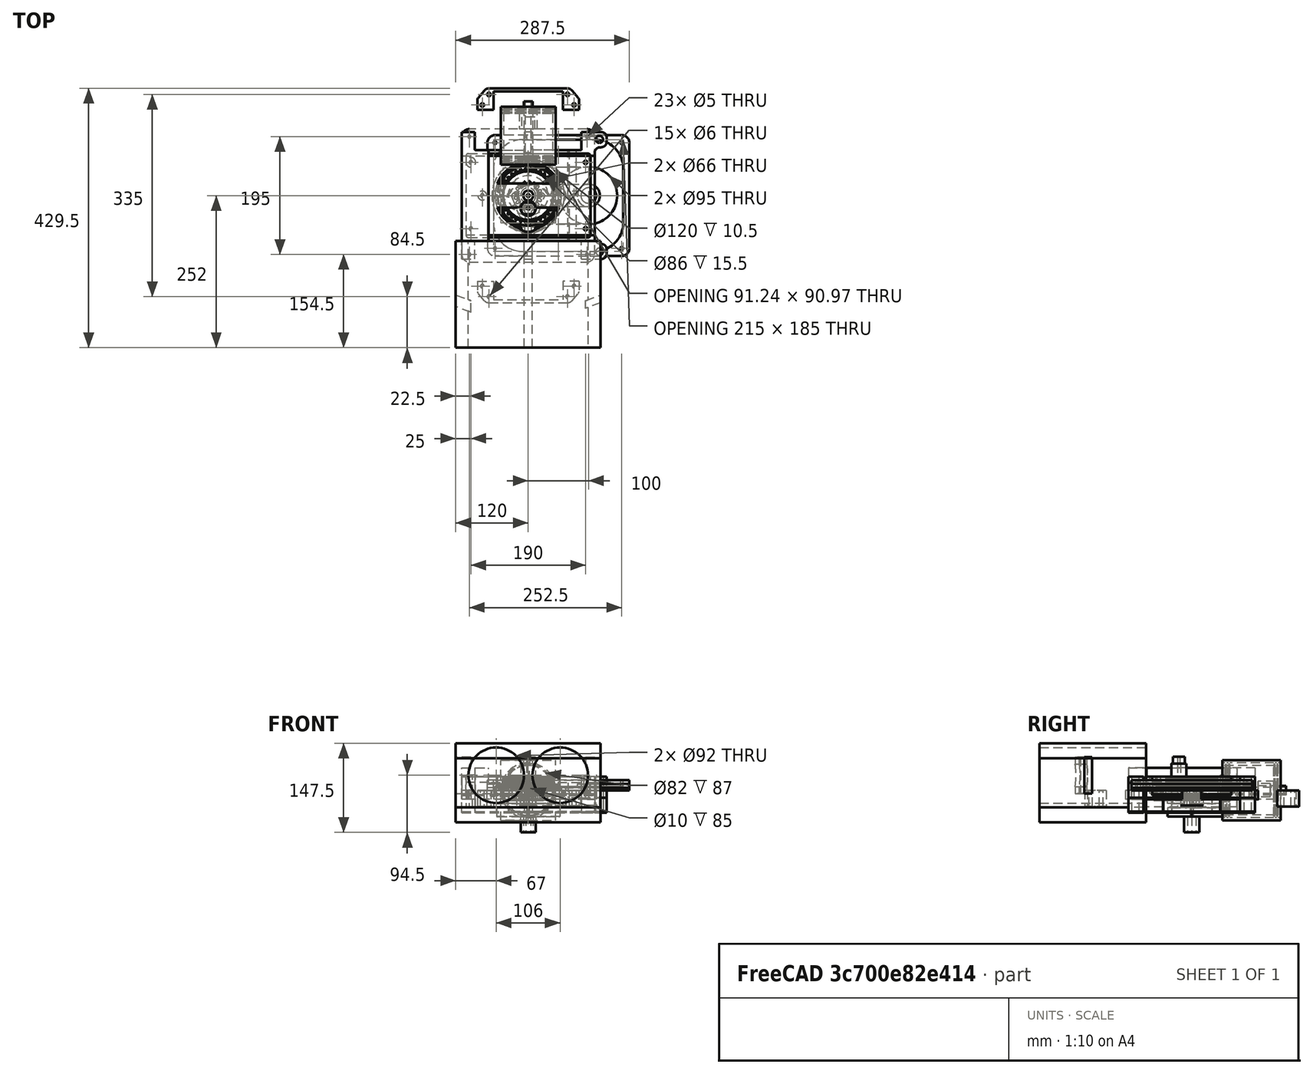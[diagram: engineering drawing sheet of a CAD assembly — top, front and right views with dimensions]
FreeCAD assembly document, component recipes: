
FREECAD ASSEMBLY — COMPONENT RECIPES ("assm4_XX_at_Tusi_rider")

This assembly document has 31 components, labeled P0..P30 below (a component is one placed body or linked part). 30 of them carry a construction recipe — the FreeCAD feature program that regenerates the part from scratch, quoted from this document or its linked companion documents; the rest are supplied as boundary geometry only. No exploded tour is included for this assembly.
COMPONENT P0 — geometry summary ("Assembly_total"; no construction recipe available for this part):
  bounding box: 314.5 x 312.0 x 154.5 mm
  tessellated surface: 128,050 triangles
  volume: 581524 mm^3 (4% of its bounding box)
COMPONENT P1 — recipe-attached ("Шток_поршня", modeled in this document).
Construction recipe (the document's own serialized feature program — sketch geometry with constraints, then the solid features built on it; lengths are millimeters unless a unit is written):

FEATURE [PartDesign::CoordinateSystem] Pin
  AttacherType = Attacher::AttachEngine3D
  AttachmentSupport = -> [XY_Plane001]
  MapMode = 5
FEATURE [Sketcher::SketchObject] Sketch053
  ArcFitTolerance = 0
  AttachmentOffset = pos=(0,0,-66) rot=(0,0,1;0rad)
  AttachmentSupport = -> [XZ_Plane001]
  FullyConstrained = true
  MakeInternals = false
  MapMode = 5
  Placement = pos=(0,66,-1.47e-14) rot=(1,0,0;1.5708rad)
  sketch-geometry (2):
    g0: Circle CenterX=0 CenterY=0 CenterZ=0 NormalX=0 NormalY=0 NormalZ=1 AngleXU=0 Radius=7.5
    g1: Circle CenterX=0 CenterY=0 CenterZ=0 NormalX=0 NormalY=0 NormalZ=1 AngleXU=0 Radius=5
  constraints (4):
    c: Coincident(g0,g-1)
    c: Coincident(g1,g0)
    c: Diameter(g0) = 15
    c: Diameter(g1) = 10
FEATURE [PartDesign::Pad] Pad
  Direction = (0,-1,2e-16)
  Length = 90
  Length2 = 1
  Placement = pos=(0,0,0) rot=(1,0,0;1.5708rad)
  Profile = -> Sketch053
  ReferenceAxis = -> Sketch053 [N_Axis]
  Reversed = true
  Suppressed = false
  Type = 0
FEATURE [Sketcher::SketchObject] Sketch055
  ArcFitTolerance = 0
  AttachmentOffset = pos=(0,0,-66) rot=(0,0,1;0rad)
  AttachmentSupport = -> [XZ_Plane001]
  FullyConstrained = true
  MakeInternals = false
  MapMode = 5
  Placement = pos=(0,66,-1.47e-14) rot=(1,0,0;1.5708rad)
  sketch-geometry (2):
    g0: Circle CenterX=0 CenterY=0 CenterZ=0 NormalX=0 NormalY=0 NormalZ=1 AngleXU=0 Radius=5
    g1: Circle CenterX=0 CenterY=0 CenterZ=0 NormalX=0 NormalY=0 NormalZ=1 AngleXU=0 Radius=2
  constraints (4):
    c: Diameter(g0) = 10
    c: Coincident(g1,g0)
    c: Coincident(g0,g-1)
    c: Diameter(g1) = 4
FEATURE [PartDesign::Pad] Pad026
  BaseFeature = -> Pad
  Direction = (0,-1,2e-16)
  Length = 5
  Length2 = 17
  Placement = pos=(0,0,0) rot=(1,0,0;1.5708rad)
  Profile = -> Sketch055
  ReferenceAxis = -> Sketch055 [N_Axis]
  Reversed = true
  Suppressed = false
  Type = 4
FEATURE [Sketcher::SketchObject] Sketch085
  ArcFitTolerance = 1e-06
  AttachmentOffset = pos=(0,0,-66) rot=(0,0,1;0rad)
  AttachmentSupport = -> [XZ_Plane001]
  ExternalGeometry = -> [Pad026]
  FullyConstrained = true
  MakeInternals = false
  MapMode = 5
  Placement = pos=(0,66,-1.47e-14) rot=(1,0,0;1.5708rad)
  sketch-geometry (7):
    g0: ArcOfCircle CenterX=0 CenterY=0 CenterZ=0 NormalX=0 NormalY=0 NormalZ=1 AngleXU=0 Radius=7.5 StartAngle=2.41186 EndAngle=3.87132
    g1: LineSegment StartX=-5.59017 StartY=5 StartZ=0 EndX=5.59017 EndY=5 EndZ=0
    g2: LineSegment StartX=-5.59017 StartY=-5 StartZ=0 EndX=5.59017 EndY=-5 EndZ=0
    g3: ArcOfCircle CenterX=0 CenterY=0 CenterZ=0 NormalX=0 NormalY=0 NormalZ=1 AngleXU=0 Radius=7.5 StartAngle=5.55346 EndAngle=7.01291
    g4: LineSegment [constr] StartX=0 StartY=5 StartZ=0 EndX=0 EndY=-5 EndZ=0
    g5: LineSegment [constr] StartX=5.59017 StartY=5 StartZ=0 EndX=5.59017 EndY=-5 EndZ=0
    g6: Circle CenterX=0 CenterY=0 CenterZ=0 NormalX=0 NormalY=0 NormalZ=1 AngleXU=0 Radius=2
  constraints (20):
    c: Coincident(g0,g-1)
    c: Horizontal(g1)
    c: Horizontal(g2)
    c: Coincident(g0,g1)
    c: Coincident(g1,g3)
    c: Equal(g0,g3)
    c: Coincident(g0,g2)
    c: Coincident(g0,g3)
    c: Equal(g3,g-3)
    c: PointOnObject(g4,g-5)
    c: PointOnObject(g4,g-5)
    c: Coincident(g5,g1)
    c: Coincident(g5,g2)
    c: Vertical(g5)
    c: Equal(g4,g5)
    c: PointOnObject(g4,g-2)
    c: Coincident(g6,g0)
    c: Equal(g6,g-4)
    c: Coincident(g2,g3)
    c: Vertical(g4)
FEATURE [PartDesign::Pad] Pad046
  BaseFeature = -> Pad026
  Direction = (0,-1,2e-16)
  Length = 2
  Length2 = 10
  Placement = pos=(0,0,0) rot=(1,0,0;1.5708rad)
  Profile = -> Sketch085
  ReferenceAxis = -> Sketch085 [N_Axis]
  Refine = true
  Suppressed = false
  Type = 0
FEATURE [PartDesign::Body] Body  label="Шток_поршня"
  AllowCompound = false
  Group = -> [Pin,Sketch053,Pad,Sketch055,Pad026,Sketch085,Pad046]
  Origin = -> Origin001
  Tip = -> Pad046
COMPONENT P2 — recipe-attached ("Эксцентрик", modeled in this document).
Construction recipe (the document's own serialized feature program — sketch geometry with constraints, then the solid features built on it; lengths are millimeters unless a unit is written):

FEATURE [Sketcher::SketchObject] Sketch005
  ArcFitTolerance = 0
  AttachmentSupport = -> [XY_Plane002]
  FullyConstrained = true
  MakeInternals = false
  MapMode = 5
  expr: Constraints[1] = <<Dim_table>>.crank_dia2 + <<Dim_table>>.zazor
  expr: Constraints[26] = 10
  expr: Constraints[27] = <<Dim_table>>.ecc_dia * 0.8
  expr: Constraints[28] = <<Dim_table>>.crank_dia2 * 2
  expr: Constraints[2] = <<Dim_table>>.ecc_dia + <<Dim_table>>.roller_dia
  expr: Constraints[3] = <<Dim_table>>.crank_len
  sketch-geometry (14):
    g0: Circle CenterX=0 CenterY=-21.25 CenterZ=0 NormalX=0 NormalY=0 NormalZ=1 AngleXU=0 Radius=41.5
    g1: Circle CenterX=0 CenterY=0 CenterZ=0 NormalX=0 NormalY=0 NormalZ=1 AngleXU=0 Radius=12.75
    g2: ArcOfCircle CenterX=0 CenterY=-21.25 CenterZ=0 NormalX=0 NormalY=0 NormalZ=1 AngleXU=0 Radius=32 StartAngle=3.32205 EndAngle=4.38515
    g3: ArcOfCircle CenterX=0 CenterY=-21.25 CenterZ=0 NormalX=0 NormalY=0 NormalZ=1 AngleXU=0 Radius=32 StartAngle=5.03963 EndAngle=6.10273
    g4: LineSegment StartX=-5 StartY=-27.5681 StartZ=0 EndX=-5 EndY=-47.7641 EndZ=0
    g5: LineSegment StartX=5 StartY=-27.5681 StartZ=0 EndX=5 EndY=-47.7641 EndZ=0
    g6: ArcOfCircle CenterX=0 CenterY=0 CenterZ=0 NormalX=0 NormalY=0 NormalZ=1 AngleXU=0 Radius=25 StartAngle=3.98424 EndAngle=4.39683
    g7: ArcOfCircle CenterX=0 CenterY=0 CenterZ=0 NormalX=0 NormalY=0 NormalZ=1 AngleXU=0 Radius=25 StartAngle=5.02794 EndAngle=5.44053
    g8: ArcOfCircle CenterX=-22.6265 CenterY=-25.3779 CenterZ=0 NormalX=0 NormalY=0 NormalZ=1 AngleXU=0 Radius=9 StartAngle=0.842651 EndAngle=3.32205
    g9: ArcOfCircle CenterX=22.6265 CenterY=-25.3779 CenterZ=0 NormalX=0 NormalY=0 NormalZ=1 AngleXU=0 Radius=9 StartAngle=6.10273 EndAngle=8.58213
    g10: ArcOfCircle CenterX=-9 CenterY=-47.7641 CenterZ=0 NormalX=0 NormalY=0 NormalZ=1 AngleXU=0 Radius=4 StartAngle=4.38515 EndAngle=6.28319
    g11: ArcOfCircle CenterX=9 CenterY=-47.7641 CenterZ=0 NormalX=0 NormalY=0 NormalZ=1 AngleXU=0 Radius=4 StartAngle=3.14159 EndAngle=5.03963
    g12: ArcOfCircle CenterX=-9 CenterY=-27.5681 CenterZ=0 NormalX=0 NormalY=0 NormalZ=1 AngleXU=0 Radius=4 StartAngle=0 EndAngle=1.25524
    g13: ArcOfCircle CenterX=9 CenterY=-27.5681 CenterZ=0 NormalX=0 NormalY=0 NormalZ=1 AngleXU=0 Radius=4 StartAngle=1.88635 EndAngle=3.14159
  constraints (32):
    c: PointOnObject(g0,g-2)
    c: Diameter(g1) = 25.5
    c: Diameter(g0) = 83
    c: Distance(g1,g0) = 21.25
    c: Coincident(g1,g-1)
    c: Coincident(g2,g0)
    c: Coincident(g3,g0)
    c: Equal(g2,g3)
    c: Vertical(g4)
    c: Coincident(g6,g1)
    c: Coincident(g7,g1)
    c: Tangent(g2,g8) = -1.5708
    c: Tangent(g6,g8) = 1.5708
    c: Tangent(g7,g9) = 1.5708
    c: Tangent(g3,g9) = -1.5708
    c: Tangent(g2,g10) = -1.5708
    c: Tangent(g4,g10) = 1.5708
    c: Tangent(g5,g11) = -1.5708
    c: Tangent(g3,g11) = -1.5708
    c: Tangent(g6,g12) = 1.5708
    c: Tangent(g4,g12) = 1.5708
    c: Tangent(g5,g13) = -1.5708
    c: Tangent(g7,g13) = 1.5708
    c: Symmetric(g12,g13,g-2)
    c: Symmetric(g10,g11,g-2)
    c: Symmetric(g8,g9,g-2)
    c: DistanceX(g4,g5) = 10
    c: Diameter(g2) = 64
    c: Diameter(g6) = 50
    c: Radius(g10) = 4
    c: Equal(g10,g12)
    c: Radius(g8) = 9
FEATURE [PartDesign::CoordinateSystem] Eccentr
  AttacherType = Attacher::AttachEngine3D
  AttachmentOffset = pos=(0,0,0) rot=(0,0,1;1.5708rad)
  AttachmentSupport = -> [Sketch005]
  MapMode = 11
  Placement = pos=(0,0,0) rot=(0,0,1;3.14159rad)
FEATURE [PartDesign::Pad] Pad001
  Direction = (0,0,1)
  Length = 16.5
  Length2 = 0
  Profile = -> Sketch005
  ReferenceAxis = -> Sketch005 [N_Axis]
  Reversed = true
  Suppressed = false
  Type = 0
  expr: Length = <<Dim_table>>.ecc_hei
FEATURE [PartDesign::SubtractiveCylinder] Cylinder003
  Angle = 360
  AttacherType = Attacher::AttachEngine3D
  AttachmentOffset = pos=(0,0,-14) rot=(0,0,1;0rad)
  AttachmentSupport = -> [Pad001]
  BaseFeature = -> Pad001
  FirstAngle = 0
  Height = 25.2
  MapMode = 2
  Placement = pos=(0,0,-14) rot=(0,0,1;0rad)
  Radius = 16
  Refine = true
  SecondAngle = 0
  Suppressed = false
FEATURE [PartDesign::SubtractiveCylinder] Cylinder008
  Angle = 360
  AttacherType = Attacher::AttachEngine3D
  AttachmentOffset = pos=(23,0,-13) rot=(0,0,1;0rad)
  AttachmentSupport = -> [XY_Plane002]
  BaseFeature = -> Cylinder003
  FirstAngle = 0
  Height = 25
  MapMode = 5
  Placement = pos=(23,0,-13) rot=(0,0,1;0rad)
  Radius = 4
  Refine = true
  SecondAngle = 0
  Suppressed = false
FEATURE [PartDesign::SubtractiveCylinder] Cylinder009
  Angle = 360
  AttacherType = Attacher::AttachEngine3D
  AttachmentOffset = pos=(-23,0,-13) rot=(0,0,1;0rad)
  AttachmentSupport = -> [XY_Plane002]
  BaseFeature = -> Cylinder008
  FirstAngle = 0
  Height = 25
  MapMode = 5
  Placement = pos=(-23,0,-13) rot=(0,0,1;0rad)
  Radius = 4
  Refine = true
  SecondAngle = 0
  Suppressed = false
FEATURE [Sketcher::SketchObject] Sketch084
  ArcFitTolerance = 1e-06
  AttachmentSupport = -> [XY_Plane002]
  FullyConstrained = true
  MakeInternals = false
  MapMode = 5
  expr: Constraints[2] = <<Dim_table>>.crank_len
  expr: Constraints[3] = <<Dim_table>>.ecc_dia
  expr: Constraints[4] = <<Dim_table>>.ecc_dia * 1.2
  sketch-geometry (2):
    g0: Circle CenterX=0 CenterY=-21.25 CenterZ=0 NormalX=0 NormalY=0 NormalZ=1 AngleXU=0 Radius=40
    g1: Circle CenterX=0 CenterY=-21.25 CenterZ=0 NormalX=0 NormalY=0 NormalZ=1 AngleXU=0 Radius=48
  constraints (5):
    c: PointOnObject(g0,g-2)
    c: Coincident(g1,g0)
    c: Distance(g0,g-1) = 21.25
    c: Diameter(g0) = 80
    c: Diameter(g1) = 96
FEATURE [PartDesign::Pocket] Pocket
  BaseFeature = -> Cylinder009
  Direction = (0,0,-1)
  Length = 15.25
  Length2 = -1.25
  Placement = pos=(-23,0,-13) rot=(0,0,1;0rad)
  Profile = -> Sketch084
  ReferenceAxis = -> Sketch084 [N_Axis]
  Refine = true
  Suppressed = false
  Type = 4
FEATURE [PartDesign::Body] Body001  label="Эксцентрик"
  AllowCompound = false
  Group = -> [Sketch005,Pad001,Eccentr,Cylinder003,Cylinder008,Cylinder009,Sketch084,Pocket]
  Origin = -> Origin002
  Tip = -> Pocket
COMPONENT P3 — recipe-attached ("Ползун_рабочий", modeled in this document).
Construction recipe (the document's own serialized feature program — sketch geometry with constraints, then the solid features built on it; lengths are millimeters unless a unit is written):

FEATURE [Sketcher::SketchObject] Sketch007
  ArcFitTolerance = 0
  AttachmentSupport = -> [XY_Plane003]
  FullyConstrained = true
  MakeInternals = false
  MapMode = 5
  expr: Constraints[15] = <<Dim_table>>.ecc_dia * 1.3
  expr: Constraints[17] = <<Dim_table>>.ecc_dia * 0.8
  expr: Constraints[1] = <<Dim_table>>.ecc_dia + 2 * <<Dim_table>>.roller_dia
  sketch-geometry (15):
    g0: Circle CenterX=0 CenterY=0 CenterZ=0 NormalX=0 NormalY=0 NormalZ=1 AngleXU=0 Radius=43
    g1: ArcOfCircle CenterX=0 CenterY=0 CenterZ=0 NormalX=0 NormalY=0 NormalZ=1 AngleXU=0 Radius=52 StartAngle=1.86916 EndAngle=3.14159
    g2: ArcOfCircle CenterX=0 CenterY=0 CenterZ=0 NormalX=0 NormalY=0 NormalZ=1 AngleXU=0 Radius=52 StartAngle=0 EndAngle=1.27243
    g3: LineSegment StartX=-11.8314 StartY=53.6134 StartZ=0 EndX=-10 EndY=64 EndZ=0
    g4: LineSegment StartX=-10 StartY=64 StartZ=0 EndX=10 EndY=64 EndZ=0
    g5: LineSegment StartX=10 StartY=64 StartZ=0 EndX=11.8314 EndY=53.6134 EndZ=0
    g6: ArcOfCircle CenterX=-16.7555 CenterY=54.4817 CenterZ=0 NormalX=0 NormalY=0 NormalZ=1 AngleXU=0 Radius=5 StartAngle=5.01075 EndAngle=6.10865
    g7: ArcOfCircle CenterX=16.7555 CenterY=54.4817 CenterZ=0 NormalX=0 NormalY=0 NormalZ=1 AngleXU=0 Radius=5 StartAngle=3.31613 EndAngle=4.41403
    g8: ArcOfCircle CenterX=-2.7e-15 CenterY=2.94305e-05 CenterZ=0 NormalX=0 NormalY=0 NormalZ=1 AngleXU=0 Radius=52 StartAngle=3.14159 EndAngle=4.41403
    g9: ArcOfCircle CenterX=-16.7555 CenterY=-54.4817 CenterZ=0 NormalX=0 NormalY=0 NormalZ=1 AngleXU=0 Radius=5 StartAngle=0.174533 EndAngle=1.27243
    g10: LineSegment StartX=-11.8314 StartY=-53.6134 StartZ=0 EndX=-10 EndY=-64 EndZ=0
    g11: LineSegment StartX=-10 StartY=-64 StartZ=0 EndX=10 EndY=-64 EndZ=0
    g12: LineSegment StartX=10 StartY=-64 StartZ=0 EndX=11.8314 EndY=-53.6134 EndZ=0
    g13: ArcOfCircle CenterX=16.7555 CenterY=-54.4817 CenterZ=0 NormalX=0 NormalY=0 NormalZ=1 AngleXU=0 Radius=5 StartAngle=1.86916 EndAngle=2.96706
    g14: ArcOfCircle CenterX=-2.7e-15 CenterY=2.94305e-05 CenterZ=0 NormalX=0 NormalY=0 NormalZ=1 AngleXU=0 Radius=52 StartAngle=5.01075 EndAngle=6.28318
  constraints (36):
    c: Coincident(g0,g-1)
    c: Diameter(g0) = 86
    c: Coincident(g1,g0)
    c: Coincident(g2,g0)
    c: Equal(g1,g2)
    c: Coincident(g3,g4)
    c: Coincident(g4,g5)
    c: Tangent(g1,g6) = 1.5708
    c: Tangent(g3,g6) = -1.5708
    c: Tangent(g5,g7) = -1.5708
    c: Tangent(g2,g7) = 1.5708
    c: Symmetric(g6,g7,g-2)
    c: Symmetric(g3,g4,g-2)
    c: PointOnObject(g1,g-1)
    c: PointOnObject(g2,g-1)
    c: Diameter(g1) = 104
    c: Distance(g4,g4) = 20
    c: DistanceY(g0,g4) = 64
    c: Radius(g6) = 5
    c: Angle(g3,g-2) = 0.174533
    c: Equal(g8,g14)
    c: Coincident(g10,g11)
    c: Coincident(g11,g12)
    c: Tangent(g8,g9) = 1.5708
    c: Tangent(g10,g9) = 1.5708
    c: Tangent(g12,g13) = 1.5708
    c: Tangent(g14,g13) = 1.5708
    c: Equal(g8,g1)
    c: Equal(g13,g7)
    c: Symmetric(g9,g13,g-2)
    c: Symmetric(g11,g4,g-1)
    c: Symmetric(g10,g11,g-2)
    c: Parallel(g12,g3)
    c: Coincident(g8,g1)
    c: Coincident(g14,g2)
    c: Coincident(g8,g14)
FEATURE [PartDesign::Pad] Pad002
  Direction = (0,0,1)
  Length = 15.5
  Length2 = 10
  Midplane = true
  Profile = -> Sketch007
  ReferenceAxis = -> Sketch007 [N_Axis]
  Suppressed = false
  Type = 0
  expr: Length = <<Dim_table>>.ecc_hei - 1
FEATURE [PartDesign::CoordinateSystem] Shtok
  AttacherType = Attacher::AttachEngine3D
  AttachmentSupport = -> [Pad002]
  MapMode = 45
  Placement = pos=(-7.2e-15,2.69855e-05,-3e-16) rot=(0,0,1;0rad)
FEATURE [Sketcher::SketchObject] Sketch
  ArcFitTolerance = 1e-06
  AttachmentSupport = -> [Pad002]
  FullyConstrained = true
  MakeInternals = false
  MapMode = 5
  Placement = pos=(0,-64,0) rot=(1,0,0;1.5708rad)
  sketch-geometry (1):
    g0: Circle CenterX=0 CenterY=0 CenterZ=0 NormalX=0 NormalY=0 NormalZ=1 AngleXU=0 Radius=0.5
  constraints (2):
    c: Coincident(g0,g-1)
    c: Diameter(g0) = 1
FEATURE [PartDesign::Hole] Hole001
  BaseFeature = -> Pad002
  CustomThreadClearance = 0
  Depth = 15
  DepthType = 0
  Diameter = 11
  DrillForDepth = false
  DrillPoint = 1
  DrillPointAngle = 118
  HoleCutCountersinkAngle = 90
  HoleCutCustomValues = false
  HoleCutDepth = 0
  HoleCutDiameter = 6.1
  HoleCutType = 0
  ModelThread = false
  Profile = -> Sketch
  Refine = true
  Suppressed = false
  Tapered = false
  TaperedAngle = 90
  ThreadClass = 0
  ThreadDepth = 15
  ThreadDepthType = 0
  ThreadDirection = 0
  ThreadFit = 0
  ThreadSize = 22
  ThreadType = 2
  Threaded = false
  UseCustomThreadClearance = false
FEATURE [Sketcher::SketchObject] Sketch083
  ArcFitTolerance = 1e-06
  AttachmentSupport = -> [Hole001]
  FullyConstrained = true
  MakeInternals = false
  MapMode = 5
  Placement = pos=(0,64,0) rot=(0,0.707107,0.707107;3.14159rad)
  sketch-geometry (1):
    g0: Circle CenterX=0 CenterY=0 CenterZ=0 NormalX=0 NormalY=0 NormalZ=1 AngleXU=0 Radius=0.5
  constraints (2):
    c: Coincident(g0,g-1)
    c: Diameter(g0) = 1
FEATURE [PartDesign::Hole] Hole002
  BaseFeature = -> Hole001
  CustomThreadClearance = 0
  Depth = 15
  DepthType = 0
  Diameter = 11
  DrillForDepth = false
  DrillPoint = 1
  DrillPointAngle = 118
  HoleCutCountersinkAngle = 90
  HoleCutCustomValues = false
  HoleCutDepth = 0
  HoleCutDiameter = 6.1
  HoleCutType = 0
  ModelThread = false
  Profile = -> Sketch083
  Refine = true
  Suppressed = false
  Tapered = false
  TaperedAngle = 90
  ThreadClass = 0
  ThreadDepth = 15
  ThreadDepthType = 0
  ThreadDirection = 0
  ThreadFit = 0
  ThreadSize = 22
  ThreadType = 2
  Threaded = false
  UseCustomThreadClearance = false
FEATURE [PartDesign::Body] Body002  label="Ползун_рабочий"
  AllowCompound = false
  Group = -> [Sketch007,Pad002,Shtok,Sketch,Hole001,Sketch083,Hole002]
  Origin = -> Origin003
  Tip = -> Hole002
COMPONENT P4 — recipe-attached ("Шейка_шатунная", modeled in this document).
Construction recipe (the document's own serialized feature program — sketch geometry with constraints, then the solid features built on it; lengths are millimeters unless a unit is written):

FEATURE [Sketcher::SketchObject] Sketch004
  ArcFitTolerance = 0
  AttachmentSupport = -> [XY_Plane004]
  FullyConstrained = true
  MakeInternals = false
  MapMode = 5
  expr: Constraints[0] = <<Dim_table>>.crank_dia2
  expr: Constraints[2] = <<Dim_table>>.crank_len
  expr: Constraints[4] = <<Dim_table>>.axle_hole_dia
  sketch-geometry (2):
    g0: Circle CenterX=0 CenterY=-21.25 CenterZ=0 NormalX=0 NormalY=0 NormalZ=1 AngleXU=0 Radius=12.5
    g1: Circle CenterX=0 CenterY=-21.25 CenterZ=0 NormalX=0 NormalY=0 NormalZ=1 AngleXU=0 Radius=2.5
  constraints (5):
    c: Diameter(g0) = 25
    c: PointOnObject(g0,g-2)
    c: DistanceY(g0,g-1) = 21.25
    c: Coincident(g1,g0)
    c: Diameter(g1) = 5
FEATURE [PartDesign::Pad] Pad003
  Direction = (0,0,1)
  Length = 79.5
  Length2 = 0
  Profile = -> Sketch004
  ReferenceAxis = -> Sketch004 [N_Axis]
  Suppressed = false
  Type = 0
FEATURE [Sketcher::SketchObject] Sketch070
  ArcFitTolerance = 0
  AttachmentSupport = -> [Pad003]
  FullyConstrained = true
  MakeInternals = false
  MapMode = 11
  Placement = pos=(0,-21.25,79.5) rot=(0,0,1;1.5708rad)
  expr: Constraints[12] = <<Dim_table>>.crank_dia2
  expr: Constraints[13] = <<Dim_table>>.axle_hole_dia
  expr: Constraints[14] = 0
  expr: Constraints[3] = <<Dim_table>>.crank_dia2 * 0.8
  sketch-geometry (5):
    g0: ArcOfCircle CenterX=0 CenterY=0 CenterZ=0 NormalX=0 NormalY=0 NormalZ=1 AngleXU=0 Radius=12.5 StartAngle=0.643501 EndAngle=2.49809
    g1: ArcOfCircle CenterX=0 CenterY=0 CenterZ=0 NormalX=0 NormalY=0 NormalZ=1 AngleXU=0 Radius=12.5 StartAngle=3.78509 EndAngle=5.63968
    g2: LineSegment StartX=10 StartY=7.5 StartZ=0 EndX=10 EndY=-7.5 EndZ=0
    g3: LineSegment StartX=-10 StartY=7.5 StartZ=0 EndX=-10 EndY=-7.5 EndZ=0
    g4: Circle CenterX=0 CenterY=0 CenterZ=0 NormalX=0 NormalY=0 NormalZ=1 AngleXU=0 Radius=2.5
  constraints (15):
    c: Coincident(g2,g0)
    c: Coincident(g2,g1)
    c: Vertical(g2)
    c: DistanceX(g0,g0) = 20
    c: Coincident(g3,g0)
    c: Coincident(g3,g1)
    c: Vertical(g3)
    c: Equal(g3,g2)
    c: Equal(g1,g0)
    c: Coincident(g1,g0)
    c: Coincident(g4,g0)
    c: PointOnObject(g0,g-2)
    c: Diameter(g0) = 25
    c: Diameter(g4) = 5
    c: DistanceY(g-1,g0) = 0
FEATURE [PartDesign::Pad] Pad038
  BaseFeature = -> Pad003
  Direction = (0,0,1)
  Length = 12
  Length2 = 10
  Profile = -> Sketch070
  ReferenceAxis = -> Sketch070 [N_Axis]
  Suppressed = false
  TaperAngle = -2
  Type = 0
FEATURE [PartDesign::Body] Body003  label="Шейка_шатунная"
  AllowCompound = false
  Group = -> [Sketch004,Pad003,Sketch070,Pad038]
  Origin = -> Origin004
  Placement = pos=(0,0,-25) rot=(0,0,1;0rad)
  Tip = -> Pad038
COMPONENT P5 — recipe-attached ("Щека", modeled in this document).
Construction recipe (the document's own serialized feature program — sketch geometry with constraints, then the solid features built on it; lengths are millimeters unless a unit is written):

FEATURE [Sketcher::SketchObject] Sketch003
  ArcFitTolerance = 0
  AttachmentSupport = -> [XY_Plane005]
  FullyConstrained = true
  MakeInternals = false
  MapMode = 5
  expr: Constraints[17] = <<Dim_table>>.fillet_r
  expr: Constraints[18] = <<Dim_table>>.fillet_r
  expr: Constraints[21] = <<Dim_table>>.inter_shaft_len - <<Dim_table>>.zazor
  expr: Constraints[23] = <<Dim_table>>.axle_hole_dia
  expr: Constraints[25] = 70
  expr: Constraints[26] = <<Dim_table>>.crank_dia2 * 1.5
  expr: Constraints[27] = <<Dim_table>>.crank_len
  sketch-geometry (14):
    g0: ArcOfCircle CenterX=0 CenterY=0 CenterZ=0 NormalX=0 NormalY=0 NormalZ=1 AngleXU=0 Radius=52.5 StartAngle=0.0396143 EndAngle=3.10198
    g1: ArcOfCircle CenterX=-1.2e-15 CenterY=-21.25 CenterZ=0 NormalX=0 NormalY=0 NormalZ=1 AngleXU=0 Radius=18.75 StartAngle=3.49066 EndAngle=5.93412
    g2: LineSegment [constr] StartX=-17.6192 StartY=-27.6629 StartZ=0 EndX=17.6192 EndY=-27.6629 EndZ=0
    g3: LineSegment StartX=-50.4604 StartY=0 StartZ=0 EndX=-29.0881 EndY=0 EndZ=0
    g4: LineSegment StartX=-27.2087 StartY=-1.31596 StartZ=0 EndX=-17.6192 EndY=-27.6629 EndZ=0
    g5: LineSegment StartX=17.6192 StartY=-27.6629 StartZ=0 EndX=27.2087 EndY=-1.31596 EndZ=0
    g6: LineSegment StartX=29.0881 StartY=-7e-16 StartZ=0 EndX=50.4604 EndY=-7e-16 EndZ=0
    g7: ArcOfCircle CenterX=-29.0881 CenterY=-2 CenterZ=0 NormalX=0 NormalY=0 NormalZ=1 AngleXU=0 Radius=2 StartAngle=0.349066 EndAngle=1.5708
    g8: ArcOfCircle CenterX=29.0881 CenterY=-2 CenterZ=0 NormalX=0 NormalY=0 NormalZ=1 AngleXU=0 Radius=2 StartAngle=1.5708 EndAngle=2.79253
    g9: ArcOfCircle CenterX=50.4604 CenterY=2 CenterZ=0 NormalX=0 NormalY=0 NormalZ=1 AngleXU=0 Radius=2 StartAngle=4.71239 EndAngle=6.3228
    g10: ArcOfCircle CenterX=-50.4604 CenterY=2 CenterZ=0 NormalX=0 NormalY=0 NormalZ=1 AngleXU=0 Radius=2 StartAngle=3.10198 EndAngle=4.71239
    g11: Circle [constr] CenterX=0 CenterY=0 CenterZ=0 NormalX=0 NormalY=0 NormalZ=1 AngleXU=0 Radius=49.75
    g12: Circle CenterX=0 CenterY=0 CenterZ=0 NormalX=0 NormalY=0 NormalZ=1 AngleXU=0 Radius=2.5
    g13: Circle [constr] CenterX=-1.2e-15 CenterY=-21.25 CenterZ=0 NormalX=0 NormalY=0 NormalZ=1 AngleXU=0 Radius=2.5
  constraints (31):
    c: Coincident(g2,g1)
    c: Coincident(g2,g1)
    c: Horizontal(g2)
    c: Horizontal(g3)
    c: Horizontal(g6)
    c: Tangent(g4,g1) = -1.5708
    c: Tangent(g5,g1) = -1.5708
    c: Tangent(g3,g7) = 1.5708
    c: Tangent(g4,g7) = 1.5708
    c: Tangent(g6,g8) = 1.5708
    c: Tangent(g5,g8) = 1.5708
    c: Tangent(g6,g9) = -1.5708
    c: Tangent(g0,g9) = -1.5708
    c: Tangent(g0,g10) = -1.5708
    c: Tangent(g3,g10) = -1.5708
    c: Symmetric(g7,g8,g-2)
    c: Symmetric(g10,g9,g-2)
    c: Radius(g10) = 2
    c: Radius(g7) = 2
    c: Coincident(g0,g-1)
    c: Coincident(g11,g0)
    c: Diameter(g11) = 99.5
    c: Coincident(g12,g11)
    c: Diameter(g12) = 5
    c: Diameter(g0) = 105
    c: Angle(g5) = 1.22173
    c: Diameter(g1) = 37.5
    c: DistanceY(g1,g12) = 21.25
    c: PointOnObject(g3,g-1)
    c: Coincident(g13,g1)
    c: Equal(g13,g12)
FEATURE [PartDesign::Pad] Pad004
  Direction = (0,0,1)
  Length = 15
  Length2 = 10
  Profile = -> Sketch003
  ReferenceAxis = -> Sketch003 [N_Axis]
  Suppressed = false
  Type = 0
FEATURE [PartDesign::Body] Body004  label="Щека"
  AllowCompound = false
  Group = -> [Sketch003,Pad004]
  Origin = -> Origin005
  Placement = pos=(0,0,12.5) rot=(0,0,1;0rad)
  Tip = -> Pad004
COMPONENT P6 — recipe-attached ("Шейка коренная", modeled in this document).
Construction recipe (the document's own serialized feature program — sketch geometry with constraints, then the solid features built on it; lengths are millimeters unless a unit is written):

FEATURE [Sketcher::SketchObject] Sketch002
  ArcFitTolerance = 0
  AttachmentSupport = -> [XY_Plane006]
  FullyConstrained = true
  MakeInternals = false
  MapMode = 5
  expr: Constraints[0] = <<Dim_table>>.crank_dia1
  expr: Constraints[20] = <<Dim_table>>.hex_size
  sketch-geometry (8):
    g0: Circle CenterX=0 CenterY=0 CenterZ=0 NormalX=0 NormalY=0 NormalZ=1 AngleXU=0 Radius=12.5
    g1: LineSegment StartX=4.04145 StartY=7 StartZ=0 EndX=-4.04145 EndY=7 EndZ=0
    g2: LineSegment StartX=-4.04145 StartY=7 StartZ=0 EndX=-8.0829 EndY=0 EndZ=0
    g3: LineSegment StartX=-8.0829 StartY=0 StartZ=0 EndX=-4.04145 EndY=-7 EndZ=0
    g4: LineSegment StartX=-4.04145 StartY=-7 StartZ=0 EndX=4.04145 EndY=-7 EndZ=0
    g5: LineSegment StartX=4.04145 StartY=-7 StartZ=0 EndX=8.0829 EndY=-9e-16 EndZ=0
    g6: LineSegment StartX=8.0829 StartY=-9e-16 StartZ=0 EndX=4.04145 EndY=7 EndZ=0
    g7: Circle [constr] CenterX=0 CenterY=0 CenterZ=0 NormalX=0 NormalY=0 NormalZ=1 AngleXU=0 Radius=8.0829
  constraints (18):
    c: Diameter(g0) = 25
    c: Coincident(g1,g2)
    c: Coincident(g2,g3)
    c: Coincident(g3,g4)
    c: Coincident(g4,g5)
    c: Coincident(g5,g6)
    c: Coincident(g6,g1)
    c: Equal(g1, g2-g6) x5
    c: PointOnObject(g1,g7)
    c: PointOnObject(g2,g7)
    c: PointOnObject(g3,g7)
    c: PointOnObject(g4,g7)
    c: PointOnObject(g5,g7)
    c: PointOnObject(g6,g7)
    c: Coincident(g7,g0)
    c: Horizontal(g1)
    c: DistanceY(g3,g1) = 14
    c: Coincident(g0,g-1)
FEATURE [PartDesign::Pad] Pad005
  Direction = (0,0,1)
  Length = 26
  Length2 = 10
  Profile = -> Sketch002
  ReferenceAxis = -> Sketch002 [N_Axis]
  Reversed = true
  Suppressed = false
  Type = 0
FEATURE [PartDesign::Body] Body005  label="Шейка коренная"
  AllowCompound = false
  Group = -> [Sketch002,Pad005]
  Origin = -> Origin006
  Placement = pos=(0,0,47) rot=(0,0,1;0rad)
  Tip = -> Pad005
COMPONENT P7 — recipe-attached ("Body052", modeled in this document).
Construction recipe (the document's own serialized feature program — sketch geometry with constraints, then the solid features built on it; lengths are millimeters unless a unit is written):

FEATURE [PartDesign::FeatureBase] Clone002
  BaseFeature = -> Body003
  Suppressed = false
FEATURE [PartDesign::Body] Body052
  AllowCompound = false
  Group = -> [Clone002]
  Origin = -> Origin053
  Placement = pos=(0,0,-35.5) rot=(0,0,1;0rad)
  Tip = -> Clone002
COMPONENT P8 — recipe-attached ("Body054", modeled in this document).
Construction recipe (the document's own serialized feature program — sketch geometry with constraints, then the solid features built on it; lengths are millimeters unless a unit is written):

FEATURE [PartDesign::FeatureBase] Clone004
  BaseFeature = -> Body005
  Suppressed = false
FEATURE [PartDesign::Body] Body054
  AllowCompound = false
  Group = -> [Clone004]
  Origin = -> Origin055
  Placement = pos=(0,0,-43.5) rot=(0,0,1;0rad)
  Tip = -> Clone004
COMPONENT P9 — recipe-attached ("Body055", modeled in this document).
Construction recipe (the document's own serialized feature program — sketch geometry with constraints, then the solid features built on it; lengths are millimeters unless a unit is written):

FEATURE [PartDesign::FeatureBase] Clone005
  BaseFeature = -> Body004
  Suppressed = false
FEATURE [PartDesign::Body] Body055
  AllowCompound = false
  Group = -> [Clone005]
  Origin = -> Origin056
  Placement = pos=(0,0,-43.5) rot=(0,0,1;0rad)
  Tip = -> Clone005
COMPONENT P10 — recipe-attached ("Колевал (секция)", modeled in this document).
Construction recipe (the document's own serialized feature program — sketch geometry with constraints, then the solid features built on it; lengths are millimeters unless a unit is written):

FEATURE [PartDesign::FeatureBase] Clone007
  BaseFeature = -> Fusion
  Suppressed = false
FEATURE [PartDesign::CoordinateSystem] Crank_shaft
  AttacherType = Attacher::AttachEngine3D
  AttachmentSupport = -> [Clone007]
  MapMode = 11
  Placement = pos=(0,0,-28.5) rot=(0,0,1;1.5708rad)
FEATURE [PartDesign::Fillet] Fillet
  Base = -> Clone007 [Edge52,Edge1]
  BaseFeature = -> Clone007
  Radius = 0.25
  Refine = true
  SupportTransform = false
  Suppressed = false
  UseAllEdges = false
FEATURE [PartDesign::Body] Body057  label="Колевал (секция)"
  AllowCompound = false
  Group = -> [Clone007,Crank_shaft,Fillet]
  Origin = -> Origin058
  Tip = -> Fillet
COMPONENT P11 — recipe-attached ("перегородка", modeled in this document).
Construction recipe (the document's own serialized feature program — sketch geometry with constraints, then the solid features built on it; lengths are millimeters unless a unit is written):

FEATURE [Sketcher::SketchObject] Sketch021
  ArcFitTolerance = 0
  AttachmentSupport = -> [XY_Plane062]
  FullyConstrained = false
  MakeInternals = false
  MapMode = 5
  sketch-geometry (30):
    g0: LineSegment [constr] StartX=-110 StartY=225 StartZ=0 EndX=110 EndY=225 EndZ=0
    g1: LineSegment [constr] StartX=110 StartY=225 StartZ=0 EndX=110 EndY=-225 EndZ=0
    g2: LineSegment [constr] StartX=110 StartY=-225 StartZ=0 EndX=-110 EndY=-225 EndZ=0
    g3: LineSegment [constr] StartX=-110 StartY=-225 StartZ=0 EndX=-110 EndY=225 EndZ=0
    g4: LineSegment [constr] StartX=-110 StartY=225 StartZ=0 EndX=-110 EndY=105 EndZ=0
    g5: LineSegment [constr] StartX=-110 StartY=105 StartZ=0 EndX=110 EndY=105 EndZ=0
    g6: LineSegment [constr] StartX=110 StartY=105 StartZ=0 EndX=110 EndY=225 EndZ=0
    g7: LineSegment [constr] StartX=-110 StartY=-225 StartZ=0 EndX=-110 EndY=-105 EndZ=0
    g8: LineSegment StartX=-110 StartY=-105 StartZ=0 EndX=110 EndY=-105 EndZ=0
    g9: LineSegment [constr] StartX=110 StartY=-105 StartZ=0 EndX=110 EndY=-225 EndZ=0
    g10: LineSegment [constr] StartX=-110 StartY=-105 StartZ=0 EndX=-110 EndY=105 EndZ=0
    g11: LineSegment StartX=110 StartY=105 StartZ=0 EndX=-110 EndY=105 EndZ=0
    g12: Circle CenterX=0 CenterY=0 CenterZ=0 NormalX=0 NormalY=0 NormalZ=1 AngleXU=0 Radius=33
    g13: LineSegment StartX=-110 StartY=105 StartZ=0 EndX=-110 EndY=0 EndZ=0
    g14: LineSegment [constr] StartX=110 StartY=-105 StartZ=0 EndX=110 EndY=105 EndZ=0
    g15: LineSegment StartX=110 StartY=105 StartZ=0 EndX=120.902 EndY=105 EndZ=0
    g16: LineSegment StartX=130 StartY=95.9016 StartZ=0 EndX=130 EndY=89.0984 EndZ=0
    g17: LineSegment StartX=120.902 StartY=80 StartZ=0 EndX=119.098 EndY=80 EndZ=0
    g18: ArcOfCircle CenterX=120.902 CenterY=95.9016 CenterZ=0 NormalX=0 NormalY=0 NormalZ=1 AngleXU=0 Radius=9.09838 StartAngle=0 EndAngle=1.5708
    g19: ArcOfCircle CenterX=120.902 CenterY=89.0984 CenterZ=0 NormalX=0 NormalY=0 NormalZ=1 AngleXU=0 Radius=9.09838 StartAngle=4.71239 EndAngle=6.28319
    g20: LineSegment StartX=110 StartY=70.9016 StartZ=0 EndX=110 EndY=0 EndZ=0
    g21: ArcOfCircle CenterX=119.098 CenterY=70.9016 CenterZ=0 NormalX=0 NormalY=0 NormalZ=1 AngleXU=0 Radius=9.09838 StartAngle=1.5708 EndAngle=3.14159
    g22: LineSegment StartX=110 StartY=-105 StartZ=0 EndX=120.902 EndY=-105 EndZ=0
    g23: LineSegment StartX=130 StartY=-95.9016 StartZ=0 EndX=130 EndY=-89.0984 EndZ=0
    g24: LineSegment StartX=120.902 StartY=-80 StartZ=0 EndX=119.098 EndY=-80 EndZ=0
    g25: ArcOfCircle CenterX=120.902 CenterY=-95.9016 CenterZ=0 NormalX=0 NormalY=0 NormalZ=1 AngleXU=0 Radius=9.09838 StartAngle=4.71239 EndAngle=6.28319
    g26: ArcOfCircle CenterX=120.902 CenterY=-89.0984 CenterZ=0 NormalX=0 NormalY=0 NormalZ=1 AngleXU=0 Radius=9.09838 StartAngle=0 EndAngle=1.5708
    g27: LineSegment StartX=110 StartY=-70.9016 StartZ=0 EndX=110 EndY=0 EndZ=0
    g28: ArcOfCircle CenterX=119.098 CenterY=-70.9016 CenterZ=0 NormalX=0 NormalY=0 NormalZ=1 AngleXU=0 Radius=9.09838 StartAngle=3.14159 EndAngle=4.71239
    g29: LineSegment StartX=-110 StartY=-105 StartZ=0 EndX=-110 EndY=0 EndZ=0
  constraints (61):
    c: Coincident(g0,g1)
    c: Coincident(g1,g2)
    c: Coincident(g2,g3)
    c: Coincident(g3,g0)
    c: Horizontal(g2)
    c: Vertical(g1)
    c: Symmetric(g0,g0,g-2)
    c: Symmetric(g0,g2,g-1)
    c: Coincident(g0,g4)
    c: PointOnObject(g4,g3)
    c: Coincident(g4,g5)
    c: PointOnObject(g5,g1)
    c: Horizontal(g5)
    c: Coincident(g6,g0)
    c: Coincident(g2,g7)
    c: PointOnObject(g7,g3)
    c: Horizontal(g8)
    c: Coincident(g9,g2)
    c: Equal(g9,g6)
    c: DistanceX(g2,g2) = 220
    c: DistanceY(g3,g3) = 450
    c: DistanceY(g9,g9) = 120
    c: Coincident(g10,g4)
    c: Coincident(g11,g10)
    c: Diameter(g12) = 66
    c: PointOnObject(g13,g-1)
    c: Vertical(g13)
    c: Vertical(g10)
    c: Vertical(g6)
    c: Coincident(g8,g9)
    c: Coincident(g8,g7)
    c: Coincident(g11,g5)
    c: Symmetric(g8,g11,g-1)
    c: Horizontal(g15)
    c: Horizontal(g17)
    c: Vertical(g16)
    c: Tangent(g15,g18) = 1.5708
    c: Tangent(g16,g18) = 1.5708
    c: Tangent(g16,g19) = 1.5708
    c: Tangent(g17,g19) = 1.5708
    c: Equal(g19,g18)
    c: Vertical(g20)
    c: Tangent(g17,g21) = -1.5708
    c: Tangent(g20,g21) = -1.5708
    c: Equal(g19,g21)
    c: Vertical(g14)
    c: Horizontal(g22)
    c: Horizontal(g24)
    c: Vertical(g23)
    c: Tangent(g22,g25) = -1.5708
    c: Tangent(g23,g25) = -1.5708
    c: Tangent(g23,g26) = -1.5708
    c: Tangent(g24,g26) = -1.5708
    c: Equal(g26,g25)
    c: Vertical(g27)
    c: Tangent(g24,g28) = 1.5708
    c: Tangent(g27,g28) = 1.5708
    c: Equal(g26,g28)
    c: Coincident(g13,g11)
    c: Coincident(g29,g8)
    c: Coincident(g29,g13)
FEATURE [Sketcher::SketchObject] Sketch022
  ArcFitTolerance = 0
  AttachmentSupport = -> [XY_Plane062]
  FullyConstrained = true
  MakeInternals = false
  MapMode = 5
  sketch-geometry (5):
    g0: LineSegment StartX=-110 StartY=-105 StartZ=0 EndX=-65.5 EndY=-105 EndZ=0
    g1: LineSegment StartX=-65.5 StartY=-105 StartZ=0 EndX=-65.5 EndY=105 EndZ=0
    g2: LineSegment StartX=-65.5 StartY=105 StartZ=0 EndX=-110 EndY=105 EndZ=0
    g3: LineSegment StartX=-110 StartY=105 StartZ=0 EndX=-110 EndY=-105 EndZ=0
    g4: LineSegment [constr] StartX=65.5 StartY=52.9337 StartZ=0 EndX=65.5 EndY=105 EndZ=0
  constraints (14):
    c: Coincident(g0,g1)
    c: Coincident(g1,g2)
    c: Coincident(g2,g3)
    c: Coincident(g3,g0)
    c: Horizontal(g0)
    c: Horizontal(g2)
    c: Vertical(g3)
    c: Vertical(g4)
    c: DistanceX(g1,g4) = 131
    c: Symmetric(g1,g4,g-2)
    c: DistanceY(g1,g1) = 210
    c: DistanceX(g0,g0) = 44.5
    c: Symmetric(g0,g1,g-1)
    c: Block(g4)
FEATURE [PartDesign::Pad] Pad012
  Direction = (0,0,1)
  Length = 35
  Length2 = 12.5
  Profile = -> Sketch021
  ReferenceAxis = -> Sketch021 [N_Axis]
  Reversed = true
  Suppressed = false
  Type = 4
FEATURE [PartDesign::Pad] Pad013
  BaseFeature = -> Pad012
  Direction = (0,0,1)
  Length = 37.5
  Length2 = -12.5
  Profile = -> Sketch022
  ReferenceAxis = -> Sketch022 [N_Axis]
  Suppressed = false
  Type = 4
FEATURE [Sketcher::SketchObject] Sketch_1
  ArcFitTolerance = 0
  FullyConstrained = false
  MakeInternals = false
  sketch-geometry (8):
    g0: Circle [constr] CenterX=0 CenterY=0 CenterZ=0 NormalX=0 NormalY=0 NormalZ=1 AngleXU=0 Radius=65.5
    g1: ArcOfCircle [constr] CenterX=0 CenterY=0 CenterZ=0 NormalX=0 NormalY=0 NormalZ=1 AngleXU=0 Radius=65.5 StartAngle=1.5708 EndAngle=4.71239
    g2: LineSegment StartX=145.598 StartY=65.5 StartZ=0 EndX=0 EndY=65.5 EndZ=0
    g3: LineSegment StartX=145.598 StartY=-65.5 StartZ=0 EndX=0 EndY=-65.5 EndZ=0
    g4: LineSegment StartX=145.598 StartY=65.5 StartZ=0 EndX=145.598 EndY=-65.5 EndZ=0
    g5: LineSegment StartX=-153.016 StartY=65.5 StartZ=0 EndX=0 EndY=65.5 EndZ=0
    g6: LineSegment StartX=-1.2e-14 StartY=-65.5 StartZ=0 EndX=-153.016 EndY=-65.5 EndZ=0
    g7: LineSegment StartX=-153.016 StartY=-65.5 StartZ=0 EndX=-153.016 EndY=65.5 EndZ=0
  constraints (18):
    c: Coincident(g0,g-1)
    c: Diameter(g0) = 131
    c: Coincident(g1,g0)
    c: PointOnObject(g1,g0)
    c: Horizontal(g2)
    c: Horizontal(g3)
    c: Tangent(g3,g1) = 1.5708
    c: Tangent(g1,g2) = -1.5708
    c: Coincident(g4,g2)
    c: Coincident(g4,g3)
    c: Vertical(g4)
    c: Coincident(g6,g7)
    c: Coincident(g7,g5)
    c: Horizontal(g5)
    c: Horizontal(g6)
    c: Vertical(g7)
    c: Coincident(g5,g2)
    c: Coincident(g6,g3)
FEATURE [PartDesign::Pocket] Pocket005
  BaseFeature = -> Pad013
  Direction = (0,0,-1)
  Length = 6.5
  Length2 = 13
  Profile = -> Sketch_1
  ReferenceAxis = -> Sketch_1 [N_Axis]
  Suppressed = false
  Type = 4
FEATURE [PartDesign::CoordinateSystem] Block_ribb
  AttacherType = Attacher::AttachEngine3D
  AttachmentSupport = -> [Pocket005]
  MapMode = 2
FEATURE [Sketcher::SketchObject] Sketch_2
  ArcFitTolerance = 0
  FullyConstrained = false
  MakeInternals = false
  sketch-geometry (44):
    g0: LineSegment StartX=-0.25 StartY=33.6074 StartZ=0 EndX=-0.25 EndY=47.5 EndZ=0
    g1: LineSegment StartX=-0.25 StartY=47.5 StartZ=0 EndX=126.736 EndY=47.5 EndZ=0
    g2: LineSegment StartX=126.736 StartY=47.5 StartZ=0 EndX=126.736 EndY=47 EndZ=0
    g3: LineSegment StartX=126.736 StartY=47 StartZ=0 EndX=0.25 EndY=47 EndZ=0
    g4: LineSegment StartX=0.25 StartY=47 StartZ=0 EndX=0.25 EndY=33.6074 EndZ=0
    g5: LineSegment StartX=0.25 StartY=33.6074 StartZ=0 EndX=-0.25 EndY=33.6074 EndZ=0
    g6: ArcOfCircle CenterX=86.75 CenterY=76.5 CenterZ=0 NormalX=0 NormalY=0 NormalZ=1 AngleXU=0 Radius=1.5 StartAngle=4.71239 EndAngle=6.28319
    g7: ArcOfCircle CenterX=8.25 CenterY=76.5 CenterZ=0 NormalX=0 NormalY=0 NormalZ=1 AngleXU=0 Radius=1.5 StartAngle=3.14159 EndAngle=4.71239
    g8: LineSegment StartX=86.75 StartY=75 StartZ=0 EndX=8.25 EndY=75 EndZ=0
    g9: LineSegment StartX=88.25 StartY=105 StartZ=0 EndX=6.75 EndY=105 EndZ=0
    g10: LineSegment StartX=6.75 StartY=105 StartZ=0 EndX=6.75 EndY=76.5 EndZ=0
    g11: LineSegment StartX=88.25 StartY=105 StartZ=0 EndX=88.25 EndY=76.5 EndZ=0
    g12: GeomPoint [constr] X=47.5 Y=105 Z=0
    g13: Circle CenterX=-118 CenterY=93 CenterZ=0 NormalX=0 NormalY=0 NormalZ=1 AngleXU=0 Radius=6
    g14: Circle CenterX=118 CenterY=93 CenterZ=0 NormalX=0 NormalY=0 NormalZ=1 AngleXU=0 Radius=6
    g15: LineSegment StartX=-0.067348 StartY=-33.6074 StartZ=0 EndX=-0.067348 EndY=-47.5 EndZ=0
    g16: LineSegment StartX=-0.067348 StartY=-47.5 StartZ=0 EndX=126.736 EndY=-47.5 EndZ=0
    g17: LineSegment StartX=126.736 StartY=-47.5 StartZ=0 EndX=126.736 EndY=-47 EndZ=0
    g18: LineSegment StartX=126.736 StartY=-47 StartZ=0 EndX=0.25 EndY=-47 EndZ=0
    g19: LineSegment StartX=0.25 StartY=-47 StartZ=0 EndX=0.25 EndY=-33.6074 EndZ=0
    g20: LineSegment StartX=0.25 StartY=-33.6074 StartZ=0 EndX=-0.067348 EndY=-33.6074 EndZ=0
    g21: ArcOfCircle CenterX=-86.75 CenterY=76.5 CenterZ=0 NormalX=0 NormalY=0 NormalZ=1 AngleXU=0 Radius=1.5 StartAngle=3.14159 EndAngle=4.71239
    g22: ArcOfCircle CenterX=-8.25 CenterY=76.5 CenterZ=0 NormalX=0 NormalY=0 NormalZ=1 AngleXU=0 Radius=1.5 StartAngle=4.71239 EndAngle=6.28319
    g23: LineSegment StartX=-86.75 StartY=75 StartZ=0 EndX=-8.25 EndY=75 EndZ=0
    g24: LineSegment StartX=-88.25 StartY=105 StartZ=0 EndX=-6.75 EndY=105 EndZ=0
    g25: LineSegment StartX=-6.75 StartY=105 StartZ=0 EndX=-6.75 EndY=76.5 EndZ=0
    g26: LineSegment StartX=-88.25 StartY=105 StartZ=0 EndX=-88.25 EndY=76.5 EndZ=0
    g27: GeomPoint [constr] X=-47.5 Y=105 Z=0
    g28: ArcOfCircle CenterX=86.75 CenterY=-76.5 CenterZ=0 NormalX=0 NormalY=0 NormalZ=1 AngleXU=0 Radius=1.5 StartAngle=0 EndAngle=1.5708
    g29: ArcOfCircle CenterX=8.25 CenterY=-76.5 CenterZ=0 NormalX=0 NormalY=0 NormalZ=1 AngleXU=0 Radius=1.5 StartAngle=1.5708 EndAngle=3.14159
    g30: LineSegment StartX=86.75 StartY=-75 StartZ=0 EndX=8.25 EndY=-75 EndZ=0
    g31: LineSegment StartX=88.25 StartY=-105 StartZ=0 EndX=6.75 EndY=-105 EndZ=0
    g32: LineSegment StartX=6.75 StartY=-105 StartZ=0 EndX=6.75 EndY=-76.5 EndZ=0
    g33: LineSegment StartX=88.25 StartY=-105 StartZ=0 EndX=88.25 EndY=-76.5 EndZ=0
    g34: GeomPoint [constr] X=47.5 Y=-105 Z=0
    g35: Circle CenterX=-118 CenterY=-93 CenterZ=0 NormalX=0 NormalY=0 NormalZ=1 AngleXU=0 Radius=6
    g36: Circle CenterX=118 CenterY=-93 CenterZ=0 NormalX=0 NormalY=0 NormalZ=1 AngleXU=0 Radius=6
    g37: ArcOfCircle CenterX=-86.75 CenterY=-76.5 CenterZ=0 NormalX=0 NormalY=0 NormalZ=1 AngleXU=0 Radius=1.5 StartAngle=1.5708 EndAngle=3.14159
    g38: ArcOfCircle CenterX=-8.25 CenterY=-76.5 CenterZ=0 NormalX=0 NormalY=0 NormalZ=1 AngleXU=0 Radius=1.5 StartAngle=0 EndAngle=1.5708
    g39: LineSegment StartX=-86.75 StartY=-75 StartZ=0 EndX=-8.25 EndY=-75 EndZ=0
    g40: LineSegment StartX=-88.25 StartY=-105 StartZ=0 EndX=-6.75 EndY=-105 EndZ=0
    g41: LineSegment StartX=-6.75 StartY=-105 StartZ=0 EndX=-6.75 EndY=-76.5 EndZ=0
    g42: LineSegment StartX=-88.25 StartY=-105 StartZ=0 EndX=-88.25 EndY=-76.5 EndZ=0
    g43: GeomPoint [constr] X=-47.5 Y=-105 Z=0
  constraints (95):
    c: Vertical(g0)
    c: Coincident(g0,g1)
    c: Horizontal(g1)
    c: Coincident(g1,g2)
    c: Coincident(g2,g3)
    c: Horizontal(g3)
    c: Coincident(g3,g4)
    c: Vertical(g4)
    c: Coincident(g4,g5)
    c: Coincident(g5,g0)
    c: Vertical(g2)
    c: DistanceY(g2,g2) = 0.5
    c: DistanceX(g5,g5) = 0.5
    c: Tangent(g6,g8) = 1.5708
    c: Tangent(g8,g7) = 1.5708
    c: Equal(g6,g7)
    c: Horizontal(g8)
    c: Horizontal(g9)
    c: Vertical(g11)
    c: Vertical(g10)
    c: Tangent(g6,g11) = 1.5708
    c: Tangent(g7,g10) = -1.5708
    c: Coincident(g11,g9)
    c: Coincident(g9,g10)
    c: Symmetric(g9,g9,g12)
    c: Radius(g7) = 1.5
    c: Distance(g7,g9) = 30
    c: Diameter(g13) = 12
    c: Symmetric(g0,g4,g-2)
    c: DistanceY(g-1,g13) = 93
    c: DistanceX(g13,g-1) = 118
    c: DistanceY(g-1,g9) = 105
    c: DistanceX(g9,g9) = 81.5
    c: DistanceX(g-1,g9) = 6.75
    c: Diameter(g14) = 12
    c: Vertical(g15)
    c: Coincident(g15,g16)
    c: Horizontal(g16)
    c: Coincident(g16,g17)
    c: Coincident(g17,g18)
    c: Horizontal(g18)
    c: Coincident(g18,g19)
    c: Vertical(g19)
    c: Coincident(g19,g20)
    c: Coincident(g20,g15)
    c: Vertical(g17)
    c: Tangent(g21,g23) = -1.5708
    c: Tangent(g23,g22) = -1.5708
    c: Equal(g21,g22)
    c: Horizontal(g23)
    c: Horizontal(g24)
    c: Vertical(g26)
    c: Vertical(g25)
    c: Tangent(g21,g26) = -1.5708
    c: Tangent(g22,g25) = 1.5708
    c: Coincident(g26,g24)
    c: Coincident(g24,g25)
    c: Symmetric(g24,g24,g27)
    c: Radius(g22) = 1.5
    c: Distance(g22,g24) = 30
    c: Tangent(g28,g30) = -1.5708
    c: Tangent(g30,g29) = -1.5708
    c: Equal(g28,g29)
    c: Horizontal(g30)
    c: Horizontal(g31)
    c: Vertical(g33)
    c: Vertical(g32)
    c: Tangent(g28,g33) = -1.5708
    c: Tangent(g29,g32) = 1.5708
    c: Coincident(g33,g31)
    c: Coincident(g31,g32)
    c: Symmetric(g31,g31,g34)
    c: Radius(g29) = 1.5
    c: Distance(g29,g31) = 30
    c: Diameter(g35) = 12
    c: Diameter(g36) = 12
    c: Tangent(g37,g39) = 1.5708
    c: Tangent(g39,g38) = 1.5708
    c: Equal(g37,g38)
    c: Horizontal(g39)
    c: Horizontal(g40)
    c: Vertical(g42)
    c: Vertical(g41)
    c: Tangent(g37,g42) = 1.5708
    c: Tangent(g38,g41) = -1.5708
    c: Coincident(g42,g40)
    c: Coincident(g40,g41)
    c: Symmetric(g40,g40,g43)
    c: Radius(g38) = 1.5
    c: Distance(g38,g40) = 30
    c: Symmetric(g19,g4,g-1)
    c: Horizontal(g20)
    c: Symmetric(g17,g2,g-1)
    c: DistanceY(g17,g17) = 0.5
    c: DistanceY(g16,g1) = 95
FEATURE [PartDesign::Pocket] Pocket006
  BaseFeature = -> Pocket005
  Direction = (0,0,-1)
  Length = 50
  Length2 = 50
  Profile = -> Sketch_2
  ReferenceAxis = -> Sketch_2 [N_Axis]
  Suppressed = false
  Type = 4
FEATURE [Sketcher::SketchObject] Sketch028
  ArcFitTolerance = 0
  FullyConstrained = true
  MakeInternals = false
  MapMode = 5
  Placement = pos=(0,-75,0) rot=(1,0,0;1.5708rad)
  sketch-geometry (1):
    g0: Circle CenterX=74 CenterY=-21.75 CenterZ=0 NormalX=0 NormalY=0 NormalZ=1 AngleXU=0 Radius=6
  constraints (3):
    c: Diameter(g0) = 12
    c: DistanceY(g0,g-1) = 21.75
    c: DistanceX(g-1,g0) = 74
FEATURE [PartDesign::Pocket] Pocket011
  BaseFeature = -> Pocket006
  Direction = (0,1,-2e-16)
  Length = 5
  Length2 = 5
  Profile = -> Sketch028
  ReferenceAxis = -> Sketch028 [N_Axis]
  Suppressed = false
  Type = 1
FEATURE [PartDesign::Body] Body061  label="перегородка"
  AllowCompound = false
  Group = -> [Sketch022,Sketch021,Pad012,Pad013,Sketch_1,Pocket005,Block_ribb,Sketch_2,Pocket006,Sketch028,Pocket011]
  Origin = -> Origin062
  Tip = -> Pocket011
COMPONENT P12 — recipe-attached ("Перегородка_передняя", modeled in this document).
Construction recipe (the document's own serialized feature program — sketch geometry with constraints, then the solid features built on it; lengths are millimeters unless a unit is written):

FEATURE [PartDesign::Pad] Pad017
  Direction = (0,0,1)
  Length = 37
  Length2 = 22.5
  Profile = -> Sketch021
  ReferenceAxis = -> Sketch021 [N_Axis]
  Reversed = true
  Suppressed = false
  Type = 4
FEATURE [PartDesign::Pocket] Pocket017
  BaseFeature = -> Pad017
  Direction = (0,0,-1)
  Length = 8.5
  Length2 = 13
  Profile = -> Sketch_1
  ReferenceAxis = -> Sketch_1 [N_Axis]
  Suppressed = false
  Type = 4
FEATURE [PartDesign::CoordinateSystem] Block_ribb001
  AttacherType = Attacher::AttachEngine3D
  AttachmentSupport = -> [Pocket017]
  MapMode = 2
FEATURE [PartDesign::Pocket] Pocket018
  BaseFeature = -> Pocket017
  Direction = (0,0,-1)
  Length = 50
  Length2 = 50
  Profile = -> Sketch_2
  ReferenceAxis = -> Sketch_2 [N_Axis]
  Suppressed = false
  Type = 4
FEATURE [PartDesign::Pocket] Pocket019
  BaseFeature = -> Pocket018
  Direction = (0,1,-2e-16)
  Length = 5
  Length2 = 5
  Profile = -> Sketch028
  ReferenceAxis = -> Sketch028 [N_Axis]
  Suppressed = false
  Type = 1
FEATURE [Sketcher::SketchObject] Sketch034
  ArcFitTolerance = 0
  AttachmentSupport = -> [XY_Plane062]
  FullyConstrained = false
  MakeInternals = false
  MapMode = 5
  sketch-geometry (4):
    g0: LineSegment StartX=-154.224 StartY=65.5 StartZ=0 EndX=161.628 EndY=65.5 EndZ=0
    g1: LineSegment StartX=161.628 StartY=65.5 StartZ=0 EndX=161.628 EndY=-65.5 EndZ=0
    g2: LineSegment StartX=161.628 StartY=-65.5 StartZ=0 EndX=-154.224 EndY=-65.5 EndZ=0
    g3: LineSegment StartX=-154.224 StartY=-65.5 StartZ=0 EndX=-154.224 EndY=65.5 EndZ=0
  constraints (9):
    c: Coincident(g0,g1)
    c: Coincident(g1,g2)
    c: Coincident(g2,g3)
    c: Coincident(g3,g0)
    c: Horizontal(g0)
    c: Horizontal(g2)
    c: Vertical(g3)
    c: Symmetric(g1,g0,g-1)
    c: DistanceY(g1,g1) = 131
FEATURE [PartDesign::Pocket] Pocket020
  BaseFeature = -> Pocket019
  Direction = (0,0,-1)
  Length = 25
  Length2 = -10.5
  Profile = -> Sketch034
  ReferenceAxis = -> Sketch034 [N_Axis]
  Reversed = true
  Suppressed = false
  Type = 4
FEATURE [PartDesign::Body] Body063  label="Перегородка_передняя"
  AllowCompound = false
  Group = -> [Pad017,Pocket017,Block_ribb001,Pocket018,Pocket019,Sketch034,Pocket020]
  Origin = -> Origin064
  Tip = -> Pocket020
COMPONENT P13 — recipe-attached ("перегородка_ползуна", modeled in this document).
Construction recipe (the document's own serialized feature program — sketch geometry with constraints, then the solid features built on it; lengths are millimeters unless a unit is written):

FEATURE [PartDesign::CoordinateSystem] Block_ribb002
  AttacherType = Attacher::AttachEngine3D
  MapMode = 2
FEATURE [PartDesign::Pad] Pad018
  Direction = (0,0,1)
  Length = 12.5
  Length2 = 12.5
  Profile = -> Sketch021
  ReferenceAxis = -> Sketch021 [N_Axis]
  Reversed = true
  Suppressed = false
  Type = 4
FEATURE [Sketcher::SketchObject] Sketch035
  ArcFitTolerance = 0
  FullyConstrained = false
  MakeInternals = false
  MapMode = 5
  sketch-geometry (9):
    g0: LineSegment [constr] StartX=-110 StartY=-105 StartZ=0 EndX=-65.5 EndY=-105 EndZ=0
    g1: LineSegment [constr] StartX=-65.5 StartY=-105 StartZ=0 EndX=-65.5 EndY=105 EndZ=0
    g2: LineSegment [constr] StartX=-65.5 StartY=105 StartZ=0 EndX=-110 EndY=105 EndZ=0
    g3: LineSegment [constr] StartX=-110 StartY=105 StartZ=0 EndX=-110 EndY=-105 EndZ=0
    g4: LineSegment [constr] StartX=65.5 StartY=52.7372 StartZ=0 EndX=65.5 EndY=105 EndZ=0
    g5: LineSegment StartX=-110 StartY=-105 StartZ=0 EndX=65.5 EndY=-105 EndZ=0
    g6: LineSegment StartX=65.5 StartY=-105 StartZ=0 EndX=65.5 EndY=105 EndZ=0
    g7: LineSegment StartX=65.5 StartY=105 StartZ=0 EndX=-110 EndY=105 EndZ=0
    g8: LineSegment StartX=-110 StartY=105 StartZ=0 EndX=-110 EndY=-105 EndZ=0
  constraints (23):
    c: Coincident(g0,g1)
    c: Coincident(g1,g2)
    c: Coincident(g2,g3)
    c: Coincident(g3,g0)
    c: Horizontal(g0)
    c: Horizontal(g2)
    c: Vertical(g3)
    c: Vertical(g4)
    c: DistanceX(g1,g4) = 131
    c: Symmetric(g1,g4,g-2)
    c: DistanceY(g1,g1) = 210
    c: DistanceX(g0,g0) = 44.5
    c: Symmetric(g0,g1,g-1)
    c: Coincident(g5,g6)
    c: Coincident(g6,g7)
    c: Coincident(g7,g8)
    c: Coincident(g8,g5)
    c: Horizontal(g5)
    c: Horizontal(g7)
    c: Vertical(g6)
    c: Vertical(g8)
    c: Coincident(g5,g0)
    c: Coincident(g6,g4)
FEATURE [Sketcher::SketchObject] Sketch_004
  ArcFitTolerance = 0
  FullyConstrained = false
  MakeInternals = false
  sketch-geometry (32):
    g0: ArcOfCircle CenterX=86.75 CenterY=76.5 CenterZ=0 NormalX=0 NormalY=0 NormalZ=1 AngleXU=0 Radius=1.5 StartAngle=4.71239 EndAngle=6.28319
    g1: ArcOfCircle CenterX=8.25 CenterY=76.5 CenterZ=0 NormalX=0 NormalY=0 NormalZ=1 AngleXU=0 Radius=1.5 StartAngle=3.14159 EndAngle=4.71239
    g2: LineSegment StartX=86.75 StartY=75 StartZ=0 EndX=8.25 EndY=75 EndZ=0
    g3: LineSegment StartX=88.25 StartY=105 StartZ=0 EndX=6.75 EndY=105 EndZ=0
    g4: LineSegment StartX=6.75 StartY=105 StartZ=0 EndX=6.75 EndY=76.5 EndZ=0
    g5: LineSegment StartX=88.25 StartY=105 StartZ=0 EndX=88.25 EndY=76.5 EndZ=0
    g6: GeomPoint [constr] X=47.5 Y=105 Z=0
    g7: Circle CenterX=-118 CenterY=93 CenterZ=0 NormalX=0 NormalY=0 NormalZ=1 AngleXU=0 Radius=6
    g8: Circle CenterX=118 CenterY=93 CenterZ=0 NormalX=0 NormalY=0 NormalZ=1 AngleXU=0 Radius=6
    g9: ArcOfCircle CenterX=-86.75 CenterY=76.5 CenterZ=0 NormalX=0 NormalY=0 NormalZ=1 AngleXU=0 Radius=1.5 StartAngle=3.14159 EndAngle=4.71239
    g10: ArcOfCircle CenterX=-8.25 CenterY=76.5 CenterZ=0 NormalX=0 NormalY=0 NormalZ=1 AngleXU=0 Radius=1.5 StartAngle=4.71239 EndAngle=6.28319
    g11: LineSegment StartX=-86.75 StartY=75 StartZ=0 EndX=-8.25 EndY=75 EndZ=0
    g12: LineSegment StartX=-88.25 StartY=105 StartZ=0 EndX=-6.75 EndY=105 EndZ=0
    g13: LineSegment StartX=-6.75 StartY=105 StartZ=0 EndX=-6.75 EndY=76.5 EndZ=0
    g14: LineSegment StartX=-88.25 StartY=105 StartZ=0 EndX=-88.25 EndY=76.5 EndZ=0
    g15: GeomPoint [constr] X=-47.5 Y=105 Z=0
    g16: ArcOfCircle CenterX=86.75 CenterY=-76.5 CenterZ=0 NormalX=0 NormalY=0 NormalZ=1 AngleXU=0 Radius=1.5 StartAngle=0 EndAngle=1.5708
    g17: ArcOfCircle CenterX=8.25 CenterY=-76.5 CenterZ=0 NormalX=0 NormalY=0 NormalZ=1 AngleXU=0 Radius=1.5 StartAngle=1.5708 EndAngle=3.14159
    g18: LineSegment StartX=86.75 StartY=-75 StartZ=0 EndX=8.25 EndY=-75 EndZ=0
    g19: LineSegment StartX=88.25 StartY=-105 StartZ=0 EndX=6.75 EndY=-105 EndZ=0
    g20: LineSegment StartX=6.75 StartY=-105 StartZ=0 EndX=6.75 EndY=-76.5 EndZ=0
    g21: LineSegment StartX=88.25 StartY=-105 StartZ=0 EndX=88.25 EndY=-76.5 EndZ=0
    g22: GeomPoint [constr] X=47.5 Y=-105 Z=0
    g23: Circle CenterX=-118 CenterY=-93 CenterZ=0 NormalX=0 NormalY=0 NormalZ=1 AngleXU=0 Radius=6
    g24: Circle CenterX=118 CenterY=-93 CenterZ=0 NormalX=0 NormalY=0 NormalZ=1 AngleXU=0 Radius=6
    g25: ArcOfCircle CenterX=-86.75 CenterY=-76.5 CenterZ=0 NormalX=0 NormalY=0 NormalZ=1 AngleXU=0 Radius=1.5 StartAngle=1.5708 EndAngle=3.14159
    g26: ArcOfCircle CenterX=-8.25 CenterY=-76.5 CenterZ=0 NormalX=0 NormalY=0 NormalZ=1 AngleXU=0 Radius=1.5 StartAngle=0 EndAngle=1.5708
    g27: LineSegment StartX=-86.75 StartY=-75 StartZ=0 EndX=-8.25 EndY=-75 EndZ=0
    g28: LineSegment StartX=-88.25 StartY=-105 StartZ=0 EndX=-6.75 EndY=-105 EndZ=0
    g29: LineSegment StartX=-6.75 StartY=-105 StartZ=0 EndX=-6.75 EndY=-76.5 EndZ=0
    g30: LineSegment StartX=-88.25 StartY=-105 StartZ=0 EndX=-88.25 EndY=-76.5 EndZ=0
    g31: GeomPoint [constr] X=-47.5 Y=-105 Z=0
  constraints (65):
    c: Tangent(g0,g2) = 1.5708
    c: Tangent(g2,g1) = 1.5708
    c: Equal(g0,g1)
    c: Horizontal(g2)
    c: Horizontal(g3)
    c: Vertical(g5)
    c: Vertical(g4)
    c: Tangent(g0,g5) = 1.5708
    c: Tangent(g1,g4) = -1.5708
    c: Coincident(g5,g3)
    c: Coincident(g3,g4)
    c: Symmetric(g3,g3,g6)
    c: Radius(g1) = 1.5
    c: Distance(g1,g3) = 30
    c: Diameter(g7) = 12
    c: DistanceY(g-1,g7) = 93
    c: DistanceX(g7,g-1) = 118
    c: DistanceY(g-1,g3) = 105
    c: DistanceX(g3,g3) = 81.5
    c: DistanceX(g-1,g3) = 6.75
    c: Diameter(g8) = 12
    c: Tangent(g9,g11) = -1.5708
    c: Tangent(g11,g10) = -1.5708
    c: Equal(g9,g10)
    c: Horizontal(g11)
    c: Horizontal(g12)
    c: Vertical(g14)
    c: Vertical(g13)
    c: Tangent(g9,g14) = -1.5708
    c: Tangent(g10,g13) = 1.5708
    c: Coincident(g14,g12)
    c: Coincident(g12,g13)
    c: Symmetric(g12,g12,g15)
    c: Radius(g10) = 1.5
    c: Distance(g10,g12) = 30
    c: Tangent(g16,g18) = -1.5708
    c: Tangent(g18,g17) = -1.5708
    c: Equal(g16,g17)
    c: Horizontal(g18)
    c: Horizontal(g19)
    c: Vertical(g21)
    c: Vertical(g20)
    c: Tangent(g16,g21) = -1.5708
    c: Tangent(g17,g20) = 1.5708
    c: Coincident(g21,g19)
    c: Coincident(g19,g20)
    c: Symmetric(g19,g19,g22)
    c: Radius(g17) = 1.5
    c: Distance(g17,g19) = 30
    c: Diameter(g23) = 12
    c: Diameter(g24) = 12
    c: Tangent(g25,g27) = 1.5708
    c: Tangent(g27,g26) = 1.5708
    c: Equal(g25,g26)
    c: Horizontal(g27)
    c: Horizontal(g28)
    c: Vertical(g30)
    c: Vertical(g29)
    c: Tangent(g25,g30) = 1.5708
    c: Tangent(g26,g29) = -1.5708
    c: Coincident(g30,g28)
    c: Coincident(g28,g29)
    c: Symmetric(g28,g28,g31)
    c: Radius(g26) = 1.5
    c: Distance(g26,g28) = 30
FEATURE [PartDesign::Pocket] Pocket021
  BaseFeature = -> Pad018
  Direction = (0,0,-1)
  Length = 20
  Length2 = 20
  Profile = -> Sketch_004
  ReferenceAxis = -> Sketch_004 [N_Axis]
  Suppressed = false
  Type = 4
FEATURE [PartDesign::Pocket] Pocket022
  BaseFeature = -> Pocket021
  Direction = (0,0,-1)
  Length = 20
  Length2 = 20
  Profile = -> Sketch035
  ReferenceAxis = -> Sketch035 [N_Axis]
  Suppressed = false
  Type = 4
FEATURE [PartDesign::Body] Body064  label="перегородка_ползуна"
  AllowCompound = false
  Group = -> [Sketch035,Pad018,Block_ribb002,Sketch_004,Pocket021,Pocket022]
  Origin = -> Origin065
  Tip = -> Pocket022
COMPONENT P14 — recipe-attached ("направляющая_орто_ползуна", modeled in this document).
Construction recipe (the document's own serialized feature program — sketch geometry with constraints, then the solid features built on it; lengths are millimeters unless a unit is written):

FEATURE [Sketcher::SketchObject] Sketch038
  ArcFitTolerance = 0
  FullyConstrained = true
  MakeInternals = false
  MapMode = 5
  sketch-geometry (26):
    g0: LineSegment [constr] StartX=-103 StartY=-65 StartZ=0 EndX=103 EndY=-65 EndZ=0
    g1: LineSegment StartX=103 StartY=-65 StartZ=0 EndX=103 EndY=65 EndZ=0
    g2: LineSegment [constr] StartX=103 StartY=65 StartZ=0 EndX=-103 EndY=65 EndZ=0
    g3: LineSegment StartX=-103 StartY=65 StartZ=0 EndX=-103 EndY=-65 EndZ=0
    g4: ArcOfCircle CenterX=0 CenterY=40 CenterZ=0 NormalX=0 NormalY=0 NormalZ=1 AngleXU=0 Radius=20.25 StartAngle=1.05267 EndAngle=2.08892
    g5: ArcOfCircle CenterX=0 CenterY=0 CenterZ=0 NormalX=0 NormalY=0 NormalZ=1 AngleXU=0 Radius=55 StartAngle=2.08892 EndAngle=4.19427
    g6: ArcOfCircle CenterX=0 CenterY=0 CenterZ=0 NormalX=0 NormalY=0 NormalZ=1 AngleXU=0 Radius=55 StartAngle=5.23051 EndAngle=7.33586
    g7: ArcOfCircle CenterX=0 CenterY=-40 CenterZ=0 NormalX=0 NormalY=0 NormalZ=1 AngleXU=0 Radius=20.25 StartAngle=4.19427 EndAngle=5.23051
    g8: LineSegment StartX=-27.2388 StartY=47.7813 StartZ=0 EndX=-10.0288 EndY=57.5922 EndZ=0
    g9: LineSegment StartX=10.0288 StartY=57.5922 StartZ=0 EndX=27.2388 EndY=47.7813 EndZ=0
    g10: LineSegment StartX=-27.2388 StartY=-47.7812 StartZ=0 EndX=-10.0288 EndY=-57.5922 EndZ=0
    g11: LineSegment StartX=10.0288 StartY=-57.5922 StartZ=0 EndX=27.2388 EndY=-47.7812 EndZ=0
    g12: LineSegment StartX=-99 StartY=69.5 StartZ=0 EndX=99 EndY=69.5 EndZ=0
    g13: LineSegment StartX=-103 StartY=65 StartZ=0 EndX=-103 EndY=65.5 EndZ=0
    g14: LineSegment StartX=103 StartY=65.5 StartZ=0 EndX=103 EndY=65 EndZ=0
    g15: ArcOfCircle CenterX=-99 CenterY=65.5 CenterZ=0 NormalX=0 NormalY=0 NormalZ=1 AngleXU=0 Radius=4 StartAngle=1.5708 EndAngle=3.14159
    g16: ArcOfCircle CenterX=99 CenterY=65.5 CenterZ=0 NormalX=0 NormalY=0 NormalZ=1 AngleXU=0 Radius=4 StartAngle=4e-16 EndAngle=1.5708
    g17: ArcOfCircle CenterX=-99 CenterY=-65.5 CenterZ=0 NormalX=0 NormalY=0 NormalZ=1 AngleXU=0 Radius=4 StartAngle=3.14159 EndAngle=4.71239
    g18: LineSegment StartX=-103 StartY=-65 StartZ=0 EndX=-103 EndY=-65.5 EndZ=0
    g19: LineSegment StartX=-99 StartY=-69.5 StartZ=0 EndX=99 EndY=-69.5 EndZ=0
    g20: ArcOfCircle CenterX=99 CenterY=-65.5 CenterZ=0 NormalX=0 NormalY=0 NormalZ=1 AngleXU=0 Radius=4 StartAngle=4.71239 EndAngle=6.28319
    g21: LineSegment StartX=103 StartY=-65.5 StartZ=0 EndX=103 EndY=-65 EndZ=0
    g22: Circle CenterX=-95 CenterY=55 CenterZ=0 NormalX=0 NormalY=0 NormalZ=1 AngleXU=0 Radius=3
    g23: Circle CenterX=95 CenterY=55 CenterZ=0 NormalX=0 NormalY=0 NormalZ=1 AngleXU=0 Radius=3
    g24: Circle CenterX=-95 CenterY=-55 CenterZ=0 NormalX=0 NormalY=0 NormalZ=1 AngleXU=0 Radius=3
    g25: Circle CenterX=95 CenterY=-55 CenterZ=0 NormalX=0 NormalY=0 NormalZ=1 AngleXU=0 Radius=3
  constraints (58):
    c: Coincident(g0,g1)
    c: Coincident(g1,g2)
    c: Coincident(g2,g3)
    c: Coincident(g3,g0)
    c: Horizontal(g0)
    c: Vertical(g1)
    c: Symmetric(g2,g1,g-2)
    c: Symmetric(g2,g0,g-1)
    c: DistanceX(g2,g2) = 206
    c: PointOnObject(g4,g-2)
    c: Diameter(g4) = 40.5
    c: Equal(g4,g7)
    c: Symmetric(g4,g7,g-1)
    c: Equal(g5,g6)
    c: Tangent(g5,g10) = -1.5708
    c: Tangent(g5,g8) = 1.5708
    c: Tangent(g4,g8) = 1.5708
    c: Tangent(g4,g9) = 1.5708
    c: Tangent(g7,g11) = -1.5708
    c: Tangent(g7,g10) = -1.5708
    c: Tangent(g6,g9) = 1.5708
    c: Tangent(g6,g11) = -1.5708
    c: Distance(g-1,g4) = 40
    c: DistanceY(g1,g1) = 130
    c: Radius(g6) = 55
    c: Coincident(g5,g-1)
    c: Coincident(g6,g5)
    c: Coincident(g13,g3)
    c: Coincident(g14,g1)
    c: Tangent(g13,g15) = 1.5708
    c: Tangent(g12,g15) = 1.5708
    c: Tangent(g12,g16) = 1.5708
    c: Tangent(g14,g16) = 1.5708
    c: Vertical(g13)
    c: Vertical(g14)
    c: Symmetric(g15,g16,g-2)
    c: DistanceY(g1,g12) = 4.5
    c: Radius(g16) = 4
    c: Tangent(g18,g17) = -1.5708
    c: Tangent(g19,g17) = -1.5708
    c: Tangent(g19,g20) = -1.5708
    c: Vertical(g18)
    c: Symmetric(g17,g20,g-2)
    c: Symmetric(g17,g15,g-1)
    c: Coincident(g18,g3)
    c: Coincident(g21,g1)
    c: Vertical(g21)
    c: Equal(g21,g18)
    c: Coincident(g20,g21)
    c: Equal(g22,g23)
    c: Equal(g23,g25)
    c: Equal(g25,g24)
    c: Diameter(g23) = 6
    c: Symmetric(g22,g23,g-2)
    c: Symmetric(g24,g25,g-2)
    c: Symmetric(g24,g22,g-1)
    c: DistanceY(g24,g22) = 110
    c: DistanceX(g24,g25) = 190
FEATURE [PartDesign::Pad] Pad020
  Direction = (0,0,1)
  Length = 22.5
  Length2 = 5.5
  Midplane = true
  Profile = -> Sketch038
  ReferenceAxis = -> Sketch038 [N_Axis]
  Suppressed = false
  Type = 4
FEATURE [PartDesign::CoordinateSystem] Shtok003
  AttacherType = Attacher::AttachEngine3D
  AttachmentSupport = -> [Sketch038]
  MapMode = 2
FEATURE [Sketcher::SketchObject] Sketch061
  ArcFitTolerance = 0
  AttachmentSupport = -> [Pad020]
  FullyConstrained = false
  MakeInternals = false
  MapMode = 5
  Placement = pos=(0,0,22.5) rot=(0,0,1;0rad)
  sketch-geometry (5):
    g0: Circle CenterX=0 CenterY=0 CenterZ=0 NormalX=0 NormalY=0 NormalZ=1 AngleXU=0 Radius=8.25
    g1: LineSegment StartX=-79.3827 StartY=20 StartZ=0 EndX=79.3827 EndY=20 EndZ=0
    g2: LineSegment StartX=79.3827 StartY=20 StartZ=0 EndX=79.3827 EndY=-20 EndZ=0
    g3: LineSegment StartX=79.3827 StartY=-20 StartZ=0 EndX=-79.3827 EndY=-20 EndZ=0
    g4: LineSegment StartX=-79.3827 StartY=-20 StartZ=0 EndX=-79.3827 EndY=20 EndZ=0
  constraints (12):
    c: Coincident(g0,g-1)
    c: Diameter(g0) = 16.5
    c: Coincident(g1,g2)
    c: Coincident(g2,g3)
    c: Coincident(g3,g4)
    c: Coincident(g4,g1)
    c: Horizontal(g1)
    c: Horizontal(g3)
    c: Vertical(g2)
    c: Vertical(g4)
    c: Symmetric(g3,g1,g0)
    c: DistanceY(g2,g2) = 40
FEATURE [PartDesign::Pad] Pad032
  BaseFeature = -> Pad020
  Direction = (0,0,1)
  Length = 16
  Length2 = 10
  Profile = -> Sketch061
  ReferenceAxis = -> Sketch061 [N_Axis]
  Reversed = true
  Suppressed = false
  Type = 0
FEATURE [PartDesign::Body] Body066  label="направляющая_орто_ползуна"
  AllowCompound = false
  Group = -> [Sketch038,Pad020,Shtok003,Sketch061,Pad032]
  Origin = -> Origin067
  Tip = -> Pad032
COMPONENT P15 — recipe-attached ("Поршень003", modeled in this document).
Construction recipe (the document's own serialized feature program — sketch geometry with constraints, then the solid features built on it; lengths are millimeters unless a unit is written):

FEATURE [Sketcher::SketchObject] Sketch041
  ArcFitTolerance = 0
  AttachmentSupport = -> [XY_Plane069]
  FullyConstrained = true
  MakeInternals = false
  MapMode = 5
  sketch-geometry (6):
    g0: Circle [constr] CenterX=0 CenterY=85 CenterZ=0 NormalX=0 NormalY=0 NormalZ=1 AngleXU=0 Radius=11.5
    g1: LineSegment StartX=-45.5 StartY=147 StartZ=0 EndX=45.5 EndY=147 EndZ=0
    g2: LineSegment StartX=-45.5 StartY=147 StartZ=0 EndX=-45.5 EndY=51 EndZ=0
    g3: LineSegment StartX=0 StartY=51 StartZ=0 EndX=-45.5 EndY=51 EndZ=0
    g4: LineSegment StartX=45.5 StartY=147 StartZ=0 EndX=45.5 EndY=51 EndZ=0
    g5: LineSegment StartX=0 StartY=51 StartZ=0 EndX=45.5 EndY=51 EndZ=0
  constraints (15):
    c: Coincident(g2,g1)
    c: Vertical(g2)
    c: Symmetric(g1,g1,g-2)
    c: DistanceX(g1,g1) = 91
    c: PointOnObject(g3,g-2)
    c: Vertical(g4)
    c: Block(g0)
    c: Coincident(g1,g4)
    c: DistanceY(g0,g1) = 62
    c: DistanceY(g3,g0) = 34
    c: Horizontal(g3)
    c: Coincident(g2,g3)
    c: Coincident(g5,g3)
    c: Coincident(g5,g4)
    c: Horizontal(g5)
FEATURE [PartDesign::Pad] Pad021
  Direction = (0,0,1)
  Length = 100
  Length2 = 10
  Midplane = true
  Profile = -> Sketch041
  ReferenceAxis = -> Sketch041 [N_Axis]
  Suppressed = false
  Type = 0
FEATURE [PartDesign::Body] Body070  label="Поршень003"
  AllowCompound = false
  Group = -> [Sketch041,Pad021]
  Origin = -> Origin071
  Tip = -> Pad021
COMPONENT P16 — recipe-attached ("Поршень_2T_92mm", modeled in this document).
Construction recipe (the document's own serialized feature program — sketch geometry with constraints, then the solid features built on it; lengths are millimeters unless a unit is written):

FEATURE [PartDesign::CoordinateSystem] Piston001
  AttacherType = Attacher::AttachEngine3D
  AttachmentSupport = -> [XZ_Plane071]
  MapMode = 2
  Placement = pos=(0,0,0) rot=(1,0,0;1.5708rad)
FEATURE [Sketcher::SketchObject] Sketch042
  ArcFitTolerance = 0
  AttachmentSupport = -> [XZ_Plane071]
  FullyConstrained = false
  MakeInternals = false
  MapMode = 5
  Placement = pos=(0,0,0) rot=(1,0,0;1.5708rad)
  sketch-geometry (2):
    g0: GeomPoint [constr] X=-87.5 Y=-1.47e-14 Z=0
    g1: Circle CenterX=0 CenterY=0 CenterZ=0 NormalX=0 NormalY=0 NormalZ=1 AngleXU=0 Radius=45.5
  constraints (2):
    c: Coincident(g1,g-1)
    c: Diameter(g1) = 91
FEATURE [PartDesign::Pad] Pad022
  Direction = (0,-1,2e-16)
  Length = 200
  Length2 = 10
  Placement = pos=(0,0,0) rot=(1,0,0;1.5708rad)
  Profile = -> Sketch042
  ReferenceAxis = -> Sketch042 [N_Axis]
  Reversed = true
  Suppressed = false
  Type = 0
FEATURE [PartDesign::Boolean] Boolean004
  BaseFeature = -> Pad022
  Group = -> [Body070]
  Suppressed = false
  Type = 2
  UsePlacement = false
FEATURE [Sketcher::SketchObject] Sketch043
  ArcFitTolerance = 0
  FullyConstrained = true
  MakeInternals = false
  MapMode = 5
  Placement = pos=(0,0,0) rot=(1,0,0;1.5708rad)
  sketch-geometry (2):
    g0: Circle CenterX=0 CenterY=0 CenterZ=0 NormalX=0 NormalY=0 NormalZ=1 AngleXU=0 Radius=41
    g1: Circle CenterX=0 CenterY=0 CenterZ=0 NormalX=0 NormalY=0 NormalZ=1 AngleXU=0 Radius=15
  constraints (4):
    c: Coincident(g0,g-1)
    c: Diameter(g0) = 82
    c: Coincident(g1,g0)
    c: Diameter(g1) = 30
FEATURE [PartDesign::Pocket] Pocket025
  BaseFeature = -> Boolean004
  Direction = (0,1,-2e-16)
  Length = 138
  Length2 = 5
  Profile = -> Sketch043
  ReferenceAxis = -> Sketch043 [N_Axis]
  Suppressed = false
  Type = 0
FEATURE [Sketcher::SketchObject] Sketch044
  ArcFitTolerance = 0
  AttachmentSupport = -> [XZ_Plane071]
  FullyConstrained = false
  MakeInternals = false
  MapMode = 5
  Placement = pos=(0,0,0) rot=(1,0,0;1.5708rad)
  sketch-geometry (3):
    g0: GeomPoint [constr] X=-87.5 Y=-1.47e-14 Z=0
    g1: Circle CenterX=0 CenterY=0 CenterZ=0 NormalX=0 NormalY=0 NormalZ=1 AngleXU=0 Radius=43
    g2: Circle CenterX=0 CenterY=0 CenterZ=0 NormalX=0 NormalY=0 NormalZ=1 AngleXU=0 Radius=47.5
  constraints (4):
    c: Coincident(g1,g-1)
    c: Coincident(g2,g1)
    c: Diameter(g1) = 86
    c: Diameter(g2) = 95
FEATURE [PartDesign::Pocket] Pocket026  label="Pocket002-ring002"
  BaseFeature = -> Pocket025
  Direction = (0,1,-2e-16)
  Length = 143
  Length2 = -141
  Profile = -> Sketch044
  ReferenceAxis = -> Sketch044 [N_Axis]
  Suppressed = false
  Type = 4
FEATURE [PartDesign::Pocket] Pocket027  label="Pocket003-ring003"
  BaseFeature = -> Pocket026
  Direction = (0,1,-2e-16)
  Length = 138
  Length2 = -136
  Profile = -> Sketch044
  ReferenceAxis = -> Sketch044 [N_Axis]
  Suppressed = false
  Type = 4
FEATURE [PartDesign::Pocket] Pocket028  label="Pocket004-komp-ring001"
  BaseFeature = -> Pocket027
  Direction = (0,1,-2e-16)
  Length = 55
  Length2 = -58
  Profile = -> Sketch044
  ReferenceAxis = -> Sketch044 [N_Axis]
  Suppressed = false
  Type = 4
FEATURE [Sketcher::SketchObject] Sketch049
  ArcFitTolerance = 0
  FullyConstrained = true
  MakeInternals = false
  MapMode = 5
  Placement = pos=(0,0,0) rot=(1,0,0;1.5708rad)
  sketch-geometry (1):
    g0: Circle CenterX=0 CenterY=0 CenterZ=0 NormalX=0 NormalY=0 NormalZ=1 AngleXU=0 Radius=30
  constraints (2):
    c: Coincident(g0,g-1)
    c: Diameter(g0) = 60
FEATURE [PartDesign::Pocket] Pocket030  label="Pocket023-conrod-polzun001"
  BaseFeature = -> Pocket028
  Direction = (0,1,-2e-16)
  Length = 110
  Length2 = 5
  Profile = -> Sketch049
  ReferenceAxis = -> Sketch049 [N_Axis]
  Suppressed = false
  Type = 0
FEATURE [PartDesign::Pocket] Pocket031  label="Pocket002-ring3"
  BaseFeature = -> Pocket030
  Direction = (0,1,-2e-16)
  Length = 63
  Length2 = -61
  Profile = -> Sketch044
  ReferenceAxis = -> Sketch044 [N_Axis]
  Suppressed = false
  Type = 4
FEATURE [Sketcher::SketchObject] Sketch052
  ArcFitTolerance = 0
  FullyConstrained = true
  MakeInternals = false
  MapMode = 5
  Placement = pos=(0,0,0) rot=(1,0,0;1.5708rad)
  sketch-geometry (1):
    g0: Circle CenterX=0 CenterY=0 CenterZ=0 NormalX=0 NormalY=0 NormalZ=1 AngleXU=0 Radius=11
  constraints (2):
    c: Coincident(g0,g-1)
    c: Diameter(g0) = 22
FEATURE [PartDesign::Pocket] Pocket032
  BaseFeature = -> Pocket031
  Direction = (0,1,-2e-16)
  Length = 130
  Length2 = 5
  Profile = -> Sketch052
  ReferenceAxis = -> Sketch052 [N_Axis]
  Suppressed = false
  Type = 4
FEATURE [PartDesign::Body] Body071  label="Поршень_2T_92mm"
  AllowCompound = false
  Group = -> [Sketch042,Pad022,Boolean004,Sketch043,Pocket025,Sketch044,Pocket026,Pocket027,Pocket028,Piston001,Sketch049,Pocket030,Pocket031,Sketch052,Pocket032]
  Origin = -> Origin072
  Tip = -> Pocket032
COMPONENT P17 — recipe-attached ("Цилиндр", modeled in this document).
Construction recipe (the document's own serialized feature program — sketch geometry with constraints, then the solid features built on it; lengths are millimeters unless a unit is written):

FEATURE [PartDesign::CoordinateSystem] Cylynder001
  AttacherType = Attacher::AttachEngine3D
  AttachmentSupport = -> [Body073]
  MapMode = 2
  Placement = pos=(0,0,25) rot=(0,0,1;0rad)
FEATURE [Sketcher::SketchObject] Sketch046
  ArcFitTolerance = 0
  AttachmentSupport = -> [XZ_Plane072]
  FullyConstrained = false
  MakeInternals = false
  MapMode = 5
  Placement = pos=(0,0,0) rot=(1,0,0;1.5708rad)
  sketch-geometry (12):
    g0: ArcOfCircle [constr] CenterX=-53 CenterY=1.3e-15 CenterZ=0 NormalX=0 NormalY=0 NormalZ=1 AngleXU=0 Radius=46 StartAngle=1.5708 EndAngle=4.71239
    g1: ArcOfCircle [constr] CenterX=0 CenterY=0 CenterZ=0 NormalX=0 NormalY=0 NormalZ=1 AngleXU=0 Radius=46 StartAngle=4.71239 EndAngle=7.85398
    g2: LineSegment [constr] StartX=-53 StartY=-46 StartZ=0 EndX=-7.1e-15 EndY=-46 EndZ=0
    g3: LineSegment [constr] StartX=1.41e-14 StartY=46 StartZ=0 EndX=-53 EndY=46 EndZ=0
    g4: LineSegment StartX=-222.305 StartY=100 StartZ=0 EndX=222.305 EndY=100 EndZ=0
    g5: LineSegment StartX=222.305 StartY=100 StartZ=0 EndX=222.305 EndY=-100 EndZ=0
    g6: LineSegment StartX=222.305 StartY=-100 StartZ=0 EndX=-222.305 EndY=-100 EndZ=0
    g7: LineSegment StartX=-222.305 StartY=-100 StartZ=0 EndX=-222.305 EndY=100 EndZ=0
    g8: Circle CenterX=-53 CenterY=1.3e-15 CenterZ=0 NormalX=0 NormalY=0 NormalZ=1 AngleXU=0 Radius=46
    g9: Circle [constr] CenterX=0 CenterY=0 CenterZ=0 NormalX=0 NormalY=0 NormalZ=1 AngleXU=0 Radius=46
    g10: Circle CenterX=53 CenterY=0 CenterZ=0 NormalX=0 NormalY=0 NormalZ=1 AngleXU=0 Radius=46
    g11: LineSegment [constr] StartX=1.41e-14 StartY=46 StartZ=0 EndX=53 EndY=46 EndZ=0
  constraints (28):
    c: Tangent(g0,g2) = -1.5708
    c: Tangent(g2,g1) = -1.5708
    c: Tangent(g1,g3) = -1.5708
    c: Tangent(g3,g0) = -1.5708
    c: Equal(g0,g1)
    c: Horizontal(g2)
    c: DistanceY(g0,g0) = 92
    c: Coincident(g4,g5)
    c: Coincident(g5,g6)
    c: Coincident(g6,g7)
    c: Coincident(g7,g4)
    c: Horizontal(g6)
    c: Vertical(g7)
    c: DistanceY(g5,g5) = 200
    c: Symmetric(g5,g4,g-1)
    c: Symmetric(g4,g4,g-2)
    c: Coincident(g8,g0)
    c: Coincident(g9,g1)
    c: Equal(g8,g0)
    c: Equal(g9,g1)
    c: Coincident(g9,g-1)
    c: PointOnObject(g10,g-1)
    c: Equal(g9,g10)
    c: Coincident(g11,g1)
    c: PointOnObject(g11,g10)
    c: Horizontal(g11)
    c: Equal(g3,g11)
    c: DistanceX(g8,g10) = 106
FEATURE [PartDesign::Pad] Pad023
  Direction = (0,-1,2e-16)
  Length = 300
  Length2 = 10
  Placement = pos=(0,0,0) rot=(1,0,0;1.5708rad)
  Profile = -> Sketch046
  ReferenceAxis = -> Sketch046 [N_Axis]
  Suppressed = false
  Type = 0
FEATURE [PartDesign::Boolean] Boolean005
  BaseFeature = -> Pad023
  Group = -> [Body073]
  Suppressed = false
  Type = 2
  UsePlacement = false
FEATURE [Sketcher::SketchObject] Sketch047
  ArcFitTolerance = 0
  AttachmentSupport = -> [XY_Plane071]
  FullyConstrained = true
  MakeInternals = false
  MapMode = 5
  sketch-geometry (2):
    g0: Circle CenterX=-137 CenterY=-90 CenterZ=0 NormalX=0 NormalY=0 NormalZ=1 AngleXU=0 Radius=30.5
    g1: Circle CenterX=137 CenterY=-90 CenterZ=0 NormalX=0 NormalY=0 NormalZ=1 AngleXU=0 Radius=30.5
  constraints (5):
    c: Diameter(g0) = 61
    c: Symmetric(g0,g1,g-2)
    c: DistanceY(g0,g-1) = 90
    c: DistanceX(g0,g1) = 274
    c: Equal(g1,g0)
FEATURE [Sketcher::SketchObject] Sketch048
  ArcFitTolerance = 0
  AttachmentSupport = -> [XY_Plane071]
  FullyConstrained = false
  MakeInternals = false
  MapMode = 5
  sketch-geometry (17):
    g0: LineSegment [constr] StartX=72.5228 StartY=-25.9373 StartZ=0 EndX=72.5228 EndY=-109 EndZ=0
    g1: LineSegment [constr] StartX=72.5228 StartY=-109 StartZ=0 EndX=-72.5228 EndY=-109 EndZ=0
    g2: LineSegment [constr] StartX=-72.5228 StartY=-109 StartZ=0 EndX=-72.5228 EndY=-25.9373 EndZ=0
    g3: LineSegment StartX=-72.5228 StartY=-25.9373 StartZ=0 EndX=-160.839 EndY=-25.9373 EndZ=0
    g4: LineSegment StartX=-160.839 StartY=-25.9373 StartZ=0 EndX=-160.839 EndY=-150.037 EndZ=0
    g5: LineSegment StartX=-160.839 StartY=-150.037 StartZ=0 EndX=-95 EndY=-174 EndZ=0
    g6: LineSegment StartX=-95 StartY=-174 StartZ=0 EndX=-95 EndY=-193.155 EndZ=0
    g7: LineSegment StartX=-95 StartY=-193.155 StartZ=0 EndX=-179.18 EndY=-162.516 EndZ=0
    g8: LineSegment StartX=-179.18 StartY=-162.516 StartZ=0 EndX=-179.18 EndY=-8.0171 EndZ=0
    g9: LineSegment StartX=-179.18 StartY=-8.0171 StartZ=0 EndX=179.18 EndY=-8.0171 EndZ=0
    g10: LineSegment StartX=179.18 StartY=-8.0171 StartZ=0 EndX=179.18 EndY=-156.131 EndZ=0
    g11: LineSegment StartX=179.18 StartY=-156.131 StartZ=0 EndX=95 EndY=-186.77 EndZ=0
    g12: LineSegment StartX=95 StartY=-186.77 StartZ=0 EndX=95 EndY=-174 EndZ=0
    g13: LineSegment StartX=95 StartY=-174 StartZ=0 EndX=160.839 EndY=-150.037 EndZ=0
    g14: LineSegment StartX=160.839 StartY=-150.037 StartZ=0 EndX=160.839 EndY=-25.9373 EndZ=0
    g15: LineSegment StartX=160.839 StartY=-25.9373 StartZ=0 EndX=72.5228 EndY=-25.9373 EndZ=0
    g16: LineSegment StartX=-72.5228 StartY=-25.9373 StartZ=0 EndX=72.5228 EndY=-25.9373 EndZ=0
  constraints (43):
    c: Coincident(g0,g1)
    c: Coincident(g1,g2)
    c: Vertical(g0)
    c: Vertical(g2)
    c: DistanceY(g0,g-1) = 109
    c: Symmetric(g1,g0,g-2)
    c: Coincident(g2,g3)
    c: Horizontal(g3)
    c: Coincident(g3,g4)
    c: Vertical(g4)
    c: Coincident(g4,g5)
    c: Coincident(g5,g6)
    c: Vertical(g6)
    c: Coincident(g6,g7)
    c: Coincident(g7,g8)
    c: Vertical(g8)
    c: Coincident(g8,g9)
    c: Coincident(g9,g10)
    c: Vertical(g10)
    c: Coincident(g10,g11)
    c: Coincident(g11,g12)
    c: Vertical(g12)
    c: Coincident(g12,g13)
    c: Coincident(g13,g14)
    c: Vertical(g14)
    c: Coincident(g14,g15)
    c: Coincident(g15,g0)
    c: Horizontal(g15)
    c: Symmetric(g8,g9,g-2)
    c: Equal(g3,g15)
    c: Parallel(g5,g7)
    c: Parallel(g13,g11)
    c: Distance(g12,g11) = 12
    c: Angle(g5) = -0.349066
    c: Angle(g13) = 0.349066
    c: Symmetric(g5,g12,g-2)
    c: DistanceX(g5,g12) = 190
    c: DistanceY(g5,g-1) = 174
    c: Block(g9)
    c: Distance(g5,g7) = 18
    c: Coincident(g16,g3)
    c: Coincident(g16,g15)
    c: Horizontal(g16)
FEATURE [PartDesign::Pocket] Pocket029
  BaseFeature = -> Boolean005
  Direction = (0,0,-1)
  Length = 60
  Length2 = 5
  Midplane = true
  Profile = -> Sketch048
  ReferenceAxis = -> Sketch048 [N_Axis]
  Suppressed = false
  Type = 0
FEATURE [Sketcher::SketchObject] Sketch050
  ArcFitTolerance = 0
  AttachmentSupport = -> [YZ_Plane072]
  FullyConstrained = false
  MakeInternals = false
  MapMode = 5
  Placement = pos=(0,0,0) rot=(0.57735,0.57735,0.57735;2.0944rad)
  sketch-geometry (4):
    g0: LineSegment StartX=-184.527 StartY=91.8627 StartZ=0 EndX=-217.963 EndY=0 EndZ=0
    g1: LineSegment StartX=-217.963 StartY=0 StartZ=0 EndX=-202 EndY=0 EndZ=0
    g2: LineSegment StartX=-202 StartY=0 StartZ=0 EndX=-168.565 EndY=91.8627 EndZ=0
    g3: LineSegment StartX=-168.565 StartY=91.8627 StartZ=0 EndX=-184.527 EndY=91.8627 EndZ=0
  constraints (11):
    c: Coincident(g0,g1)
    c: Horizontal(g1)
    c: Coincident(g1,g2)
    c: Coincident(g2,g3)
    c: Coincident(g3,g0)
    c: Horizontal(g3)
    c: Equal(g1,g3)
    c: Angle(g2) = 1.22173
    c: Distance(g1,g0) = 15
    c: PointOnObject(g1,g-1)
    c: DistanceX(g1,g-1) = 202
FEATURE [PartDesign::Body] Body072  label="Цилиндр"
  AllowCompound = false
  Group = -> [Sketch046,Pad023,Boolean005,Cylynder001,Sketch047,Sketch048,Pocket029,Sketch050]
  Origin = -> Origin073
  Placement = pos=(0,0,25) rot=(0,0,1;0rad)
  Tip = -> Pocket029
COMPONENT P18 — recipe-attached ("Body073", modeled in this document).
Construction recipe (the document's own serialized feature program — sketch geometry with constraints, then the solid features built on it; lengths are millimeters unless a unit is written):

FEATURE [Sketcher::SketchObject] Sketch045
  ArcFitTolerance = 0
  AttachmentSupport = -> [XY_Plane072]
  FullyConstrained = true
  MakeInternals = false
  MapMode = 5
  sketch-geometry (11):
    g0: LineSegment [constr] StartX=-120 StartY=252 StartZ=0 EndX=120 EndY=252 EndZ=0
    g1: LineSegment [constr] StartX=120 StartY=252 StartZ=0 EndX=120 EndY=-252 EndZ=0
    g2: LineSegment StartX=120 StartY=-252 StartZ=0 EndX=-120 EndY=-252 EndZ=0
    g3: LineSegment [constr] StartX=-120 StartY=-252 StartZ=0 EndX=-120 EndY=252 EndZ=0
    g4: LineSegment [constr] StartX=-120 StartY=252 StartZ=0 EndX=-120 EndY=75.5 EndZ=0
    g5: LineSegment [constr] StartX=-120 StartY=75.5 StartZ=0 EndX=120 EndY=75.5 EndZ=0
    g6: LineSegment [constr] StartX=120 StartY=75.5 StartZ=0 EndX=120 EndY=252 EndZ=0
    g7: LineSegment StartX=-120 StartY=-252 StartZ=0 EndX=-120 EndY=-75.5 EndZ=0
    g8: LineSegment StartX=-120 StartY=-75.5 StartZ=0 EndX=120 EndY=-75.5 EndZ=0
    g9: LineSegment [constr] StartX=120 StartY=-75.5 StartZ=0 EndX=120 EndY=-252 EndZ=0
    g10: LineSegment StartX=120 StartY=-75.5 StartZ=0 EndX=120 EndY=-252 EndZ=0
  constraints (28):
    c: Coincident(g0,g1)
    c: Coincident(g1,g2)
    c: Coincident(g2,g3)
    c: Coincident(g3,g0)
    c: Horizontal(g2)
    c: Vertical(g1)
    c: Symmetric(g0,g0,g-2)
    c: Symmetric(g0,g2,g-1)
    c: Coincident(g0,g4)
    c: PointOnObject(g4,g3)
    c: Coincident(g4,g5)
    c: PointOnObject(g5,g1)
    c: Horizontal(g5)
    c: Coincident(g5,g6)
    c: Coincident(g6,g0)
    c: Coincident(g2,g7)
    c: PointOnObject(g7,g3)
    c: Coincident(g7,g8)
    c: PointOnObject(g8,g1)
    c: Horizontal(g8)
    c: Coincident(g8,g9)
    c: Coincident(g9,g2)
    c: Equal(g9,g6)
    c: DistanceX(g2,g2) = 240
    c: Coincident(g10,g8)
    c: Coincident(g10,g2)
    c: DistanceY(g2,g-1) = 252
    c: DistanceY(g7,g7) = 176.5
FEATURE [PartDesign::Pad] Pad024
  Direction = (0,0,1)
  Length = 28
  Length2 = 78
  Midplane = true
  Profile = -> Sketch045
  ReferenceAxis = -> Sketch045 [N_Axis]
  Suppressed = false
  Type = 4
FEATURE [PartDesign::Body] Body073
  AllowCompound = false
  Group = -> [Sketch045,Pad024]
  Origin = -> Origin074
  Placement = pos=(0,0,25) rot=(0,0,1;0rad)
  Tip = -> Pad024
COMPONENT P19 — recipe-attached ("корпус_нижний", modeled in this document).
Construction recipe (the document's own serialized feature program — sketch geometry with constraints, then the solid features built on it; lengths are millimeters unless a unit is written):

FEATURE [Sketcher::SketchObject] Sketch060
  ArcFitTolerance = 0
  FullyConstrained = true
  MakeInternals = false
  Placement = pos=(0,0,0) rot=(1,0,0;3.14159rad)
  expr: Constraints[11] = <<Dim_table>>.crank_dia1 + <<Dim_table>>.zazor
  expr: Constraints[14] = <<Dim_table>>.crank_dia2
  expr: Constraints[15] = <<Dim_table>>.inter_shaft_len / 2
  expr: Constraints[6] = <<Dim_table>>.inter_shaft_len
  expr: Constraints[7] = <<Dim_table>>.crank_dia1 * 1.5
  sketch-geometry (7):
    g0: ArcOfCircle CenterX=0 CenterY=0 CenterZ=0 NormalX=0 NormalY=0 NormalZ=1 AngleXU=0 Radius=18.75 StartAngle=1.5708 EndAngle=4.71239
    g1: ArcOfCircle CenterX=100 CenterY=-1.6e-15 CenterZ=0 NormalX=0 NormalY=0 NormalZ=1 AngleXU=0 Radius=18.75 StartAngle=4.71239 EndAngle=7.85398
    g2: LineSegment StartX=-3.4e-15 StartY=-18.75 StartZ=0 EndX=100 EndY=-18.75 EndZ=0
    g3: LineSegment StartX=100 StartY=18.75 StartZ=0 EndX=1.42e-14 EndY=18.75 EndZ=0
    g4: Circle CenterX=0 CenterY=0 CenterZ=0 NormalX=0 NormalY=0 NormalZ=1 AngleXU=0 Radius=12.75
    g5: Circle CenterX=100 CenterY=-1.6e-15 CenterZ=0 NormalX=0 NormalY=0 NormalZ=1 AngleXU=0 Radius=12.75
    g6: Circle CenterX=50 CenterY=0 CenterZ=0 NormalX=0 NormalY=0 NormalZ=1 AngleXU=0 Radius=12.5
  constraints (16):
    c: Tangent(g0,g2) = -1.5708
    c: Tangent(g2,g1) = -1.5708
    c: Tangent(g1,g3) = -1.5708
    c: Tangent(g3,g0) = -1.5708
    c: Equal(g0,g1)
    c: Horizontal(g2)
    c: DistanceX(g0,g1) = 100
    c: Diameter(g0) = 37.5
    c: Coincident(g4,g0)
    c: Coincident(g5,g1)
    c: Equal(g4,g5)
    c: Diameter(g4) = 25.5
    c: Coincident(g0,g-1)
    c: PointOnObject(g6,g-1)
    c: Diameter(g6) = 25
    c: DistanceX(g0,g6) = 50
FEATURE [Sketcher::SketchObject] Sketch064
  ArcFitTolerance = 0
  FullyConstrained = true
  MakeInternals = false
  Placement = pos=(0,0,0) rot=(1,0,0;3.14159rad)
  expr: Constraints[1] = <<Dim_table>>.inter_shaft_len * 1.2
  sketch-geometry (1):
    g0: Circle CenterX=0 CenterY=0 CenterZ=0 NormalX=0 NormalY=0 NormalZ=1 AngleXU=0 Radius=60
  constraints (2):
    c: Coincident(g0,g-1)
    c: Diameter(g0) = 120
FEATURE [Sketcher::SketchObject] Sketch074
  ArcFitTolerance = 0
  AttachmentSupport = -> [XY_Plane076]
  FullyConstrained = true
  MakeInternals = false
  MapMode = 5
  expr: Constraints[14] = <<Dim_table>>.ecc_dia * 1.2
  expr: Constraints[33] = <<Dim_table>>.crank_dia2
  expr: Constraints[34] = <<Dim_table>>.inter_shaft_len * 2.2
  expr: Constraints[46] = <<Dim_table>>.axle_hole_dia
  expr: Constraints[48] = 32
  expr: Constraints[53] = <<Dim_table>>.inter_shaft_len * 1.8
  sketch-geometry (25):
    g0: LineSegment [constr] StartX=-42 StartY=-90 StartZ=0 EndX=42 EndY=-90 EndZ=0
    g1: LineSegment [constr] StartX=90 StartY=-42 StartZ=0 EndX=90 EndY=42 EndZ=0
    g2: LineSegment [constr] StartX=42 StartY=90 StartZ=0 EndX=-42 EndY=90 EndZ=0
    g3: LineSegment [constr] StartX=-90 StartY=42 StartZ=0 EndX=-90 EndY=-42 EndZ=0
    g4: ArcOfCircle [constr] CenterX=-42 CenterY=42 CenterZ=0 NormalX=0 NormalY=0 NormalZ=1 AngleXU=0 Radius=48 StartAngle=1.5708 EndAngle=3.14159
    g5: ArcOfCircle [constr] CenterX=42 CenterY=42 CenterZ=0 NormalX=0 NormalY=0 NormalZ=1 AngleXU=0 Radius=48 StartAngle=1e-16 EndAngle=1.5708
    g6: ArcOfCircle [constr] CenterX=-42 CenterY=-42 CenterZ=0 NormalX=0 NormalY=0 NormalZ=1 AngleXU=0 Radius=48 StartAngle=3.14159 EndAngle=4.71239
    g7: ArcOfCircle [constr] CenterX=42 CenterY=-42 CenterZ=0 NormalX=0 NormalY=0 NormalZ=1 AngleXU=0 Radius=48 StartAngle=4.71239 EndAngle=6.28319
    g8: LineSegment [constr] StartX=-90 StartY=-42 StartZ=0 EndX=90 EndY=42 EndZ=0
    g9: GeomPoint [constr] X=0 Y=0 Z=0
    g10: ArcOfCircle CenterX=-97.5 CenterY=97.5 CenterZ=0 NormalX=0 NormalY=0 NormalZ=1 AngleXU=0 Radius=12.5 StartAngle=1.5708 EndAngle=3.14159
    g11: LineSegment StartX=97.5 StartY=110 StartZ=0 EndX=-97.5 EndY=110 EndZ=0
    g12: ArcOfCircle CenterX=97.5 CenterY=97.5 CenterZ=0 NormalX=0 NormalY=0 NormalZ=1 AngleXU=0 Radius=12.5 StartAngle=4.16e-13 EndAngle=1.5708
    g13: LineSegment StartX=110 StartY=-97.5 StartZ=0 EndX=110 EndY=97.5 EndZ=0
    g14: ArcOfCircle CenterX=97.5 CenterY=-97.5 CenterZ=0 NormalX=0 NormalY=0 NormalZ=1 AngleXU=0 Radius=12.5 StartAngle=4.71239 EndAngle=6.28319
    g15: LineSegment StartX=-97.5 StartY=-110 StartZ=0 EndX=97.5 EndY=-110 EndZ=0
    g16: ArcOfCircle CenterX=-97.5 CenterY=-97.5 CenterZ=0 NormalX=0 NormalY=0 NormalZ=1 AngleXU=0 Radius=12.5 StartAngle=3.14159 EndAngle=4.71239
    g17: LineSegment StartX=-110 StartY=97.5 StartZ=0 EndX=-110 EndY=-97.5 EndZ=0
    g18: LineSegment [constr] StartX=-97.5 StartY=110 StartZ=0 EndX=97.5 EndY=-110 EndZ=0
    g19: GeomPoint [constr] X=0 Y=0 Z=0
    g20: Circle CenterX=-97.5 CenterY=97.5 CenterZ=0 NormalX=0 NormalY=0 NormalZ=1 AngleXU=0 Radius=2.5
    g21: Circle CenterX=97.5 CenterY=97.5 CenterZ=0 NormalX=0 NormalY=0 NormalZ=1 AngleXU=0 Radius=2.5
    g22: Circle CenterX=-97.5 CenterY=-97.5 CenterZ=0 NormalX=0 NormalY=0 NormalZ=1 AngleXU=0 Radius=2.5
    g23: Circle CenterX=97.5 CenterY=-97.5 CenterZ=0 NormalX=0 NormalY=0 NormalZ=1 AngleXU=0 Radius=2.5
    g24: Circle CenterX=0 CenterY=0 CenterZ=0 NormalX=0 NormalY=0 NormalZ=1 AngleXU=0 Radius=16
  constraints (54):
    c: Horizontal(g0)
    c: Horizontal(g2)
    c: Vertical(g1)
    c: Vertical(g3)
    c: Tangent(g2,g4) = -1.5708
    c: Tangent(g3,g4) = -1.5708
    c: Tangent(g2,g5) = -1.5708
    c: Tangent(g1,g5) = -1.5708
    c: Tangent(g3,g6) = -1.5708
    c: Tangent(g0,g6) = -1.5708
    c: Tangent(g0,g7) = -1.5708
    c: Tangent(g1,g7) = -1.5708
    c: Equal(g4,g5)
    c: Equal(g5,g7)
    c: Diameter(g4) = 96
    c: Symmetric(g2,g0,g-1)
    c: Coincident(g8,g3)
    c: Coincident(g8,g1)
    c: PointOnObject(g9,g8)
    c: Horizontal(g15)
    c: Horizontal(g11)
    c: Vertical(g13)
    c: Vertical(g17)
    c: Tangent(g11,g10) = -1.5708
    c: Tangent(g17,g10) = -1.5708
    c: Tangent(g11,g12) = -1.5708
    c: Tangent(g13,g12) = -1.5708
    c: Tangent(g17,g16) = -1.5708
    c: Tangent(g15,g16) = -1.5708
    c: Tangent(g15,g14) = -1.5708
    c: Tangent(g13,g14) = -1.5708
    c: Equal(g10,g12)
    c: Equal(g12,g14)
    c: Diameter(g10) = 25
    c: DistanceY(g15,g11) = 220
    c: Symmetric(g10,g16,g-1)
    c: Coincident(g18,g10)
    c: Coincident(g18,g14)
    c: PointOnObject(g19,g18)
    c: Coincident(g20,g10)
    c: Coincident(g21,g12)
    c: Coincident(g22,g16)
    c: Coincident(g23,g14)
    c: Equal(g22,g23)
    c: Equal(g23,g21)
    c: Equal(g21,g20)
    c: Diameter(g20) = 5
    c: Coincident(g24,g9)
    c: Diameter(g24) = 32
    c: Coincident(g9,g19)
    c: Coincident(g-1,g9)
    c: Equal(g11,g13)
    c: Equal(g2,g1)
    c: DistanceX(g3,g1) = 180
FEATURE [PartDesign::CoordinateSystem] Shtok004
  AttacherType = Attacher::AttachEngine3D
  AttachmentSupport = -> [Sketch074]
  MapMode = 2
FEATURE [PartDesign::Pad] Pad042
  Direction = (0,0,1)
  Length = 15
  Length2 = 10
  Profile = -> Sketch074
  ReferenceAxis = -> Sketch074 [N_Axis]
  Reversed = true
  Suppressed = false
  Type = 0
FEATURE [PartDesign::Pad] Pad043
  BaseFeature = -> Pad042
  Direction = (0,-1e-16,-1)
  Length = 25
  Length2 = 10
  Profile = -> Sketch060
  ReferenceAxis = -> Sketch060 [N_Axis]
  Suppressed = false
  Type = 0
FEATURE [PartDesign::Pocket] Pocket036
  BaseFeature = -> Pad043
  Direction = (0,1e-16,1)
  Length = 10.5
  Length2 = 5
  Profile = -> Sketch064
  ReferenceAxis = -> Sketch064 [N_Axis]
  Reversed = true
  Suppressed = false
  Type = 0
FEATURE [PartDesign::Body] Body076  label="корпус_нижний"
  AllowCompound = false
  Group = -> [Shtok004,Sketch060,Sketch064,Sketch074,Pad042,Pad043,Pocket036]
  Origin = -> Origin077
  Tip = -> Pocket036
COMPONENT P20 — recipe-attached ("проставка_корпуса", modeled in this document).
Construction recipe (the document's own serialized feature program — sketch geometry with constraints, then the solid features built on it; lengths are millimeters unless a unit is written):

FEATURE [Sketcher::SketchObject] Sketch058
  ArcFitTolerance = 0
  AttachmentSupport = -> [XY_Plane077]
  FullyConstrained = false
  MakeInternals = false
  MapMode = 5
  sketch-geometry (32):
    g0: LineSegment [constr] StartX=-103 StartY=-65 StartZ=0 EndX=103 EndY=-65 EndZ=0
    g1: LineSegment [constr] StartX=103 StartY=-65 StartZ=0 EndX=103 EndY=65 EndZ=0
    g2: LineSegment [constr] StartX=103 StartY=65 StartZ=0 EndX=-103 EndY=65 EndZ=0
    g3: LineSegment [constr] StartX=-103 StartY=65 StartZ=0 EndX=-103 EndY=-65 EndZ=0
    g4: LineSegment [constr] StartX=-99 StartY=69.5 StartZ=0 EndX=99 EndY=69.5 EndZ=0
    g5: LineSegment [constr] StartX=-103 StartY=65 StartZ=0 EndX=-103 EndY=65.5 EndZ=0
    g6: LineSegment [constr] StartX=103 StartY=65.5 StartZ=0 EndX=103 EndY=65 EndZ=0
    g7: ArcOfCircle [constr] CenterX=-99 CenterY=65.5 CenterZ=0 NormalX=0 NormalY=0 NormalZ=1 AngleXU=0 Radius=4 StartAngle=1.5708 EndAngle=3.14159
    g8: ArcOfCircle [constr] CenterX=99 CenterY=65.5 CenterZ=0 NormalX=0 NormalY=0 NormalZ=1 AngleXU=0 Radius=4 StartAngle=-9e-16 EndAngle=1.5708
    g9: ArcOfCircle [constr] CenterX=-99 CenterY=-65.5 CenterZ=0 NormalX=0 NormalY=0 NormalZ=1 AngleXU=0 Radius=4 StartAngle=3.14159 EndAngle=4.71239
    g10: LineSegment [constr] StartX=-103 StartY=-65 StartZ=0 EndX=-103 EndY=-65.5 EndZ=0
    g11: LineSegment [constr] StartX=-99 StartY=-69.5 StartZ=0 EndX=99 EndY=-69.5 EndZ=0
    g12: ArcOfCircle [constr] CenterX=99 CenterY=-65.5 CenterZ=0 NormalX=0 NormalY=0 NormalZ=1 AngleXU=0 Radius=4 StartAngle=4.71239 EndAngle=6.28319
    g13: LineSegment [constr] StartX=103 StartY=-65.5 StartZ=0 EndX=103 EndY=-65 EndZ=0
    g14: Circle CenterX=-95 CenterY=55 CenterZ=0 NormalX=0 NormalY=0 NormalZ=1 AngleXU=0 Radius=3
    g15: Circle [constr] CenterX=95 CenterY=55 CenterZ=0 NormalX=0 NormalY=0 NormalZ=1 AngleXU=0 Radius=3
    g16: Circle [constr] CenterX=-95 CenterY=-55 CenterZ=0 NormalX=0 NormalY=0 NormalZ=1 AngleXU=0 Radius=3
    g17: Circle [constr] CenterX=95 CenterY=-55 CenterZ=0 NormalX=0 NormalY=0 NormalZ=1 AngleXU=0 Radius=3
    g18: Circle [constr] CenterX=0 CenterY=0 CenterZ=0 NormalX=0 NormalY=0 NormalZ=1 AngleXU=0 Radius=32.25
    g19: LineSegment [constr] StartX=-103 StartY=-65 StartZ=0 EndX=-91.9993 EndY=-65 EndZ=0
    g20: LineSegment [constr] StartX=-91.9993 StartY=-65 StartZ=0 EndX=-91.9993 EndY=-49.9993 EndZ=0
    g21: LineSegment [constr] StartX=-91.9993 StartY=-49.9993 StartZ=0 EndX=-103 EndY=-49.9993 EndZ=0
    g22: LineSegment [constr] StartX=-103 StartY=-49.9993 StartZ=0 EndX=-103 EndY=-65 EndZ=0
    g23: LineSegment [constr] StartX=103 StartY=-65 StartZ=0 EndX=91.9993 EndY=-65 EndZ=0
    g24: LineSegment [constr] StartX=91.9993 StartY=-65 StartZ=0 EndX=91.9993 EndY=-49.9993 EndZ=0
    g25: LineSegment [constr] StartX=91.9993 StartY=-49.9993 StartZ=0 EndX=103 EndY=-49.9993 EndZ=0
    g26: LineSegment [constr] StartX=103 StartY=-49.9993 StartZ=0 EndX=103 EndY=-65 EndZ=0
    g27: LineSegment [constr] StartX=103 StartY=65 StartZ=0 EndX=91.9993 EndY=65 EndZ=0
    g28: LineSegment [constr] StartX=91.9993 StartY=65 StartZ=0 EndX=91.9993 EndY=49.9993 EndZ=0
    g29: LineSegment [constr] StartX=91.9993 StartY=49.9993 StartZ=0 EndX=103 EndY=49.9993 EndZ=0
    g30: LineSegment [constr] StartX=103 StartY=49.9993 StartZ=0 EndX=103 EndY=65 EndZ=0
    g31: Circle CenterX=-95 CenterY=55 CenterZ=0 NormalX=0 NormalY=0 NormalZ=1 AngleXU=0 Radius=8
  constraints (75):
    c: Coincident(g0,g1)
    c: Coincident(g1,g2)
    c: Coincident(g2,g3)
    c: Coincident(g3,g0)
    c: Horizontal(g0)
    c: Vertical(g1)
    c: Symmetric(g2,g1,g-2)
    c: Symmetric(g2,g0,g-1)
    c: DistanceX(g2,g2) = 206
    c: DistanceY(g1,g1) = 130
    c: Coincident(g5,g3)
    c: Coincident(g6,g1)
    c: Tangent(g5,g7) = 1.5708
    c: Tangent(g4,g7) = 1.5708
    c: Tangent(g4,g8) = 1.5708
    c: Tangent(g6,g8) = 1.5708
    c: Vertical(g5)
    c: Vertical(g6)
    c: Symmetric(g7,g8,g-2)
    c: DistanceY(g1,g4) = 4.5
    c: Radius(g8) = 4
    c: Tangent(g10,g9) = -1.5708
    c: Tangent(g11,g9) = -1.5708
    c: Tangent(g11,g12) = -1.5708
    c: Vertical(g10)
    c: Symmetric(g9,g12,g-2)
    c: Symmetric(g9,g7,g-1)
    c: Coincident(g10,g3)
    c: Coincident(g13,g1)
    c: Vertical(g13)
    c: Equal(g13,g10)
    c: Coincident(g12,g13)
    c: Equal(g14,g15)
    c: Equal(g15,g17)
    c: Equal(g17,g16)
    c: Diameter(g15) = 6
    c: Symmetric(g14,g15,g-2)
    c: Symmetric(g16,g17,g-2)
    c: Symmetric(g16,g14,g-1)
    c: DistanceY(g16,g14) = 110
    c: DistanceX(g16,g17) = 190
    c: Coincident(g18,g-1)
    c: Diameter(g18) = 64.5
    c: Coincident(g19,g20)
    c: Coincident(g20,g21)
    c: Coincident(g21,g22)
    c: Coincident(g22,g19)
    c: Horizontal(g19)
    c: Horizontal(g21)
    c: Vertical(g20)
    c: Vertical(g22)
    c: Coincident(g19,g0)
    c: Coincident(g23,g24)
    c: Coincident(g24,g25)
    c: Coincident(g25,g26)
    c: Coincident(g26,g23)
    c: Horizontal(g23)
    c: Horizontal(g25)
    c: Vertical(g24)
    c: Vertical(g26)
    c: Coincident(g23,g0)
    c: Coincident(g27,g28)
    c: Coincident(g28,g29)
    c: Coincident(g29,g30)
    c: Coincident(g30,g27)
    c: Horizontal(g27)
    c: Horizontal(g29)
    c: Vertical(g28)
    c: Vertical(g30)
    c: Coincident(g27,g1)
    c: Equal(g25,g29)
    c: Equal(g28,g24)
    c: Equal(g24,g20)
    c: Coincident(g31,g14)
    c: Tangent(g31,g3)
FEATURE [PartDesign::Pad] Pad029
  Direction = (0,0,1)
  Length = 25
  Length2 = 28.5
  Midplane = true
  Profile = -> Sketch058
  ReferenceAxis = -> Sketch058 [N_Axis]
  Suppressed = false
  Type = 4
FEATURE [PartDesign::CoordinateSystem] Shtok005
  AttacherType = Attacher::AttachEngine3D
  AttachmentSupport = -> [Sketch058]
  MapMode = 2
FEATURE [PartDesign::Body] Body077  label="проставка_корпуса"
  AllowCompound = false
  Group = -> [Sketch058,Pad029,Shtok005]
  Origin = -> Origin078
  Tip = -> Pad029
COMPONENT P21 — recipe-attached ("crank_gear_01", modeled in this document).
Construction recipe (the document's own serialized feature program — sketch geometry with constraints, then the solid features built on it; lengths are millimeters unless a unit is written):

FEATURE [PartDesign::FeatureBase] BaseFeature
  BaseFeature = -> InvoluteGear006
  Suppressed = false
FEATURE [PartDesign::CoordinateSystem] Local_CS005
  AttacherType = Attacher::AttachEngine3D
  AttachmentOffset = pos=(0,0,0) rot=(0,0,1;0.279253rad)
  AttachmentSupport = -> [BaseFeature]
  MapMode = 2
  Placement = pos=(0,0,0) rot=(0,0,1;0.279253rad)
FEATURE [PartDesign::AdditiveCylinder] Cylinder004
  Angle = 360
  AttacherType = Attacher::AttachEngine3D
  AttachmentOffset = pos=(0,0,-0.5) rot=(0,0,1;0rad)
  AttachmentSupport = -> [BaseFeature]
  BaseFeature = -> BaseFeature
  FirstAngle = 0
  Height = 11
  MapMode = 2
  Placement = pos=(0,0,-0.5) rot=(0,0,1;0rad)
  Radius = 17
  Refine = true
  SecondAngle = 0
  Suppressed = false
FEATURE [PartDesign::SubtractiveCylinder] Cylinder005
  Angle = 360
  AttacherType = Attacher::AttachEngine3D
  AttachmentOffset = pos=(0,0,-3) rot=(0,0,1;0rad)
  AttachmentSupport = -> [BaseFeature]
  BaseFeature = -> Cylinder004
  FirstAngle = 0
  Height = 15
  MapMode = 2
  Placement = pos=(0,0,-3) rot=(0,0,1;0rad)
  Radius = 12.75
  Refine = true
  SecondAngle = 0
  Suppressed = false
FEATURE [PartDesign::Body] Body087  label="crank_gear_01"
  AllowCompound = false
  BaseFeature = -> InvoluteGear006
  Group = -> [BaseFeature,Local_CS005,Cylinder004,Cylinder005]
  Origin = -> Origin090
  Tip = -> Cylinder005
COMPONENT P22 — recipe-attached ("crank_int_gear_01", modeled in this document).
Construction recipe (the document's own serialized feature program — sketch geometry with constraints, then the solid features built on it; lengths are millimeters unless a unit is written):

FEATURE [PartDesign::FeatureBase] BaseFeature001
  BaseFeature = -> InternalInvoluteGear001
  Suppressed = false
FEATURE [PartDesign::CoordinateSystem] Local_CS004
  AttacherType = Attacher::AttachEngine3D
  AttachmentSupport = -> [BaseFeature001]
  MapMode = 2
FEATURE [PartDesign::Body] Body088  label="crank_int_gear_01"
  AllowCompound = false
  BaseFeature = -> InternalInvoluteGear001
  Group = -> [BaseFeature001,Local_CS004]
  Origin = -> Origin091
  Tip = -> BaseFeature001
COMPONENT P23 — recipe-attached ("Шейка_и_щека_задняя", modeled in this document).
Construction recipe (the document's own serialized feature program — sketch geometry with constraints, then the solid features built on it; lengths are millimeters unless a unit is written):

FEATURE [Sketcher::SketchObject] Sketch071
  ArcFitTolerance = 0
  FullyConstrained = true
  MakeInternals = false
  MapMode = 5
  expr: Constraints[0] = <<Dim_table>>.crank_dia2
  expr: Constraints[3] = <<Dim_table>>.axle_hole_dia
  sketch-geometry (2):
    g0: Circle CenterX=0 CenterY=0 CenterZ=0 NormalX=0 NormalY=0 NormalZ=1 AngleXU=0 Radius=12.5
    g1: Circle CenterX=0 CenterY=0 CenterZ=0 NormalX=0 NormalY=0 NormalZ=1 AngleXU=0 Radius=2.5
  constraints (4):
    c: Diameter(g0) = 25
    c: Coincident(g0,g-1)
    c: Coincident(g1,g0)
    c: Diameter(g1) = 5
FEATURE [PartDesign::Pad] Pad039
  Direction = (0,0,1)
  Length = 26
  Length2 = 10
  Profile = -> Sketch071
  ReferenceAxis = -> Sketch071 [N_Axis]
  Suppressed = false
  Type = 0
FEATURE [Sketcher::SketchObject] Sketch072
  ArcFitTolerance = 0
  AttachmentSupport = -> [XY_Plane094]
  FullyConstrained = true
  MakeInternals = false
  MapMode = 5
  expr: Constraints[17] = <<Dim_table>>.fillet_r
  expr: Constraints[18] = <<Dim_table>>.fillet_r
  expr: Constraints[23] = <<Dim_table>>.axle_hole_dia
  expr: Constraints[24] = 70
  expr: Constraints[25] = <<Dim_table>>.crank_dia2 * 1.5
  expr: Constraints[26] = <<Dim_table>>.crank_len
  sketch-geometry (14):
    g0: ArcOfCircle CenterX=0 CenterY=0 CenterZ=0 NormalX=0 NormalY=0 NormalZ=1 AngleXU=0 Radius=52.5 StartAngle=0.0396143 EndAngle=3.10198
    g1: ArcOfCircle CenterX=3e-16 CenterY=-21.25 CenterZ=0 NormalX=0 NormalY=0 NormalZ=1 AngleXU=0 Radius=18.75 StartAngle=3.49066 EndAngle=5.93412
    g2: LineSegment [constr] StartX=-17.6192 StartY=-27.6629 StartZ=0 EndX=17.6192 EndY=-27.6629 EndZ=0
    g3: LineSegment StartX=-50.4604 StartY=0 StartZ=0 EndX=-29.0881 EndY=0 EndZ=0
    g4: LineSegment StartX=-27.2087 StartY=-1.31596 StartZ=0 EndX=-17.6192 EndY=-27.6629 EndZ=0
    g5: LineSegment StartX=17.6192 StartY=-27.6629 StartZ=0 EndX=27.2087 EndY=-1.31596 EndZ=0
    g6: LineSegment StartX=29.0881 StartY=2.9e-15 StartZ=0 EndX=50.4604 EndY=2.9e-15 EndZ=0
    g7: ArcOfCircle CenterX=-29.0881 CenterY=-2 CenterZ=0 NormalX=0 NormalY=0 NormalZ=1 AngleXU=0 Radius=2 StartAngle=0.349066 EndAngle=1.5708
    g8: ArcOfCircle CenterX=29.0881 CenterY=-2 CenterZ=0 NormalX=0 NormalY=0 NormalZ=1 AngleXU=0 Radius=2 StartAngle=1.5708 EndAngle=2.79253
    g9: ArcOfCircle CenterX=50.4604 CenterY=2 CenterZ=0 NormalX=0 NormalY=0 NormalZ=1 AngleXU=0 Radius=2 StartAngle=4.71239 EndAngle=6.3228
    g10: ArcOfCircle CenterX=-50.4604 CenterY=2 CenterZ=0 NormalX=0 NormalY=0 NormalZ=1 AngleXU=0 Radius=2 StartAngle=3.10198 EndAngle=4.71239
    g11: Circle [constr] CenterX=0 CenterY=0 CenterZ=0 NormalX=0 NormalY=0 NormalZ=1 AngleXU=0 Radius=52.5
    g12: Circle CenterX=0 CenterY=0 CenterZ=0 NormalX=0 NormalY=0 NormalZ=1 AngleXU=0 Radius=2.5
    g13: Circle CenterX=3e-16 CenterY=-21.25 CenterZ=0 NormalX=0 NormalY=0 NormalZ=1 AngleXU=0 Radius=2.5
  constraints (31):
    c: Coincident(g2,g1)
    c: Coincident(g2,g1)
    c: Horizontal(g2)
    c: Horizontal(g3)
    c: Horizontal(g6)
    c: Tangent(g4,g1) = -1.5708
    c: Tangent(g5,g1) = -1.5708
    c: Tangent(g3,g7) = 1.5708
    c: Tangent(g4,g7) = 1.5708
    c: Tangent(g6,g8) = 1.5708
    c: Tangent(g5,g8) = 1.5708
    c: Tangent(g6,g9) = -1.5708
    c: Tangent(g0,g9) = -1.5708
    c: Tangent(g0,g10) = -1.5708
    c: Tangent(g3,g10) = -1.5708
    c: Symmetric(g7,g8,g-2)
    c: Symmetric(g10,g9,g-2)
    c: Radius(g10) = 2
    c: Radius(g7) = 2
    c: Coincident(g0,g-1)
    c: Coincident(g11,g0)
    c: Diameter(g11) = 105
    c: Coincident(g12,g11)
    c: Diameter(g12) = 5
    c: Angle(g5) = 1.22173
    c: Diameter(g1) = 37.5
    c: DistanceY(g1,g12) = 21.25
    c: PointOnObject(g3,g-1)
    c: Coincident(g13,g1)
    c: Equal(g13,g12)
    c: Equal(g0,g11)
FEATURE [PartDesign::Pad] Pad040
  BaseFeature = -> Pad039
  Direction = (0,0,1)
  Length = 15
  Length2 = 10
  Profile = -> Sketch072
  ReferenceAxis = -> Sketch072 [N_Axis]
  Reversed = true
  Suppressed = false
  Type = 0
FEATURE [PartDesign::Chamfer] Chamfer001
  Angle = 45
  Base = -> Pad040 [Edge14]
  BaseFeature = -> Pad040
  ChamferType = 0
  FlipDirection = false
  Size = 1.5
  Size2 = 1
  SupportTransform = false
  Suppressed = false
  UseAllEdges = false
FEATURE [PartDesign::Body] Body090  label="Шейка_и_щека_задняя"
  AllowCompound = false
  Group = -> [Sketch071,Pad039,Sketch072,Pad040,Chamfer001]
  Origin = -> Origin093
  Placement = pos=(0,0,-6.5) rot=(0,0,1;0rad)
  Tip = -> Chamfer001
COMPONENT P24 — recipe-attached ("Шейка_и_щека_задняя_cl", modeled in this document).
Construction recipe (the document's own serialized feature program — sketch geometry with constraints, then the solid features built on it; lengths are millimeters unless a unit is written):

FEATURE [PartDesign::FeatureBase] Clone
  BaseFeature = -> Cut
  Suppressed = false
FEATURE [PartDesign::CoordinateSystem] LCS_2
  AttacherType = Attacher::AttachEngine3D
  AttachmentSupport = -> [Cut]
  MapMode = 11
  Placement = pos=(0,0,-21.5) rot=(0,0,1;1.5708rad)
FEATURE [PartDesign::Fillet] Fillet001
  Base = -> Clone [Edge12]
  BaseFeature = -> Clone
  Radius = 0.25
  Refine = true
  SupportTransform = false
  Suppressed = false
  UseAllEdges = false
FEATURE [PartDesign::Body] Body091  label="Шейка_и_щека_задняя_cl"
  AllowCompound = false
  Group = -> [Clone,LCS_2,Fillet001]
  Origin = -> Origin094
  Tip = -> Fillet001
COMPONENT P25 — recipe-attached ("проставка_корпуса_штока1", modeled in this document).
Construction recipe (the document's own serialized feature program — sketch geometry with constraints, then the solid features built on it; lengths are millimeters unless a unit is written):

FEATURE [PartDesign::FeatureBase] BaseFeature003
  BaseFeature = -> Extrude001
  Suppressed = false
FEATURE [PartDesign::CoordinateSystem] LCS_3
  AttacherType = Attacher::AttachEngine3D
  AttachmentSupport = -> [BaseFeature003]
  MapMode = 2
FEATURE [PartDesign::Body] Body092  label="проставка_корпуса_штока1"
  AllowCompound = false
  BaseFeature = -> Extrude001
  Group = -> [BaseFeature003,LCS_3]
  Origin = -> Origin096
  Tip = -> BaseFeature003
COMPONENT P26 — recipe-attached ("ролик_3*13,8  - 87шт.", modeled in this document).
Construction recipe (the document's own serialized feature program — sketch geometry with constraints, then the solid features built on it; lengths are millimeters unless a unit is written):

FEATURE [PartDesign::AdditiveCylinder] Cylinder
  Angle = 360
  AttacherType = Attacher::AttachEngine3D
  AttachmentOffset = pos=(41.5,0,6.9) rot=(0,0,1;0rad)
  AttachmentSupport = -> [XY_Plane099]
  FirstAngle = 0
  Height = 13.8
  MapMode = 5
  Placement = pos=(41.5,0,6.9) rot=(0,0,1;0rad)
  Radius = 1.5
  Refine = true
  SecondAngle = 0
  Suppressed = false
  expr: .AttachmentOffset.Base.x = <<Dim_table>>.ecc_dia / 2 + 3 / 2
  expr: .AttachmentOffset.Base.z = 13.8 / 2
FEATURE [PartDesign::PolarPattern] PolarPattern
  Angle = 360
  Axis = -> Z_Axis097
  BaseFeature = -> Cylinder
  Mode = 0
  Occurrences = 87
  Offset = 120
  Originals = -> [Cylinder]
  Placement = pos=(41.5,0,6.9) rot=(0,0,1;0rad)
  Refine = true
  Suppressed = false
  TransformMode = 1
FEATURE [PartDesign::CoordinateSystem] LCS_4
  AttacherType = Attacher::AttachEngine3D
  AttachmentSupport = -> [Z_Axis097]
  MapMode = 7
  Placement = pos=(0,0,0) rot=(0,1,0;3.14159rad)
FEATURE [PartDesign::Body] Body094  label="ролик_3*13,8  - 87шт."
  AllowCompound = false
  Group = -> [Cylinder,PolarPattern,LCS_4]
  Origin = -> Origin098
  Tip = -> PolarPattern
COMPONENT P27 — recipe-attached ("Подшипник 942/25", modeled in this document).
Construction recipe (the document's own serialized feature program — sketch geometry with constraints, then the solid features built on it; lengths are millimeters unless a unit is written):

FEATURE [PartDesign::AdditiveCylinder] Cylinder006
  Angle = 360
  AttacherType = Attacher::AttachEngine3D
  FirstAngle = 0
  Height = 22
  MapMode = 2
  Radius = 16
  Refine = true
  SecondAngle = 0
  Suppressed = false
FEATURE [PartDesign::SubtractiveCylinder] Cylinder007
  Angle = 360
  AttacherType = Attacher::AttachEngine3D
  AttachmentSupport = -> [XY_Plane101]
  BaseFeature = -> Cylinder006
  FirstAngle = 0
  Height = 25
  MapMode = 5
  Radius = 12.5
  Refine = true
  SecondAngle = 0
  Suppressed = false
FEATURE [PartDesign::CoordinateSystem] LCS_1
  AttacherType = Attacher::AttachEngine3D
FEATURE [PartDesign::Body] Body095  label="Подшипник 942/25"
  AllowCompound = false
  Group = -> [Cylinder006,Cylinder007,LCS_1]
  Origin = -> Origin100
  Tip = -> Cylinder007
COMPONENT P28 — recipe-attached ("проставка_корпуса_с_шестернями", modeled in this document).
Construction recipe (the document's own serialized feature program — sketch geometry with constraints, then the solid features built on it; lengths are millimeters unless a unit is written):

FEATURE [Sketcher::SketchObject] Sketch075
  ArcFitTolerance = 0
  AttachmentSupport = -> [XY_Plane096]
  FullyConstrained = true
  MakeInternals = false
  MapMode = 5
  expr: Constraints[14] = <<Dim_table>>.inter_shaft_len * 2.15
  expr: Constraints[15] = <<Dim_table>>.ecc_dia * 1.2
  expr: Constraints[16] = <<Dim_table>>.inter_shaft_len * 1.85
  expr: Constraints[22] = <<Dim_table>>.inter_shaft_len / 2
  expr: Constraints[37] = <<Dim_table>>.inter_shaft_len * 2.35
  expr: Constraints[38] = <<Dim_table>>.crank_dia2
  expr: Constraints[39] = <<Dim_table>>.inter_shaft_len * 2
  expr: Constraints[45] = <<Dim_table>>.inter_shaft_len / 2
  expr: Constraints[53] = <<Dim_table>>.axle_hole_dia
  expr: Constraints[56] = <<Dim_table>>.inter_shaft_len
  expr: Constraints[58] = <<Dim_table>>.inter_shaft_len * 0.95
  sketch-geometry (26):
    g0: LineSegment [constr] StartX=-9.5 StartY=-92.5 StartZ=0 EndX=109.5 EndY=-92.5 EndZ=0
    g1: LineSegment [constr] StartX=157.5 StartY=-44.5 StartZ=0 EndX=157.5 EndY=44.5 EndZ=0
    g2: LineSegment [constr] StartX=109.5 StartY=92.5 StartZ=0 EndX=-9.5 EndY=92.5 EndZ=0
    g3: LineSegment [constr] StartX=-57.5 StartY=44.5 StartZ=0 EndX=-57.5 EndY=-44.5 EndZ=0
    g4: ArcOfCircle [constr] CenterX=-9.5 CenterY=44.5 CenterZ=0 NormalX=0 NormalY=0 NormalZ=1 AngleXU=0 Radius=48 StartAngle=1.5708 EndAngle=3.14159
    g5: ArcOfCircle [constr] CenterX=109.5 CenterY=44.5 CenterZ=0 NormalX=0 NormalY=0 NormalZ=1 AngleXU=0 Radius=48 StartAngle=0 EndAngle=1.5708
    g6: ArcOfCircle [constr] CenterX=-9.5 CenterY=-44.5 CenterZ=0 NormalX=0 NormalY=0 NormalZ=1 AngleXU=0 Radius=48 StartAngle=3.14159 EndAngle=4.71239
    g7: ArcOfCircle [constr] CenterX=109.5 CenterY=-44.5 CenterZ=0 NormalX=0 NormalY=0 NormalZ=1 AngleXU=0 Radius=48 StartAngle=4.71239 EndAngle=6.28319
    g8: LineSegment [constr] StartX=-57.5 StartY=-44.5 StartZ=0 EndX=157.5 EndY=44.5 EndZ=0
    g9: GeomPoint [constr] X=50 Y=0 Z=0
    g10: ArcOfCircle CenterX=-55 CenterY=87.5 CenterZ=0 NormalX=0 NormalY=0 NormalZ=1 AngleXU=0 Radius=12.5 StartAngle=1.5708 EndAngle=3.14159
    g11: LineSegment StartX=155 StartY=100 StartZ=0 EndX=-55 EndY=100 EndZ=0
    g12: ArcOfCircle CenterX=155 CenterY=87.5 CenterZ=0 NormalX=0 NormalY=0 NormalZ=1 AngleXU=0 Radius=12.5 StartAngle=7.01e-14 EndAngle=1.5708
    g13: LineSegment StartX=167.5 StartY=-87.5 StartZ=0 EndX=167.5 EndY=87.5 EndZ=0
    g14: ArcOfCircle CenterX=155 CenterY=-87.5 CenterZ=0 NormalX=0 NormalY=0 NormalZ=1 AngleXU=0 Radius=12.5 StartAngle=4.71239 EndAngle=6.28319
    g15: LineSegment StartX=-55 StartY=-100 StartZ=0 EndX=155 EndY=-100 EndZ=0
    g16: ArcOfCircle CenterX=-55 CenterY=-87.5 CenterZ=0 NormalX=0 NormalY=0 NormalZ=1 AngleXU=0 Radius=12.5 StartAngle=3.14159 EndAngle=4.71239
    g17: LineSegment StartX=-67.5 StartY=87.5 StartZ=0 EndX=-67.5 EndY=-87.5 EndZ=0
    g18: LineSegment [constr] StartX=-55 StartY=100 StartZ=0 EndX=155 EndY=-100 EndZ=0
    g19: GeomPoint [constr] X=50 Y=0 Z=0
    g20: Circle CenterX=-55 CenterY=87.5 CenterZ=0 NormalX=0 NormalY=0 NormalZ=1 AngleXU=0 Radius=2.5
    g21: Circle CenterX=155 CenterY=87.5 CenterZ=0 NormalX=0 NormalY=0 NormalZ=1 AngleXU=0 Radius=2.5
    g22: Circle CenterX=-55 CenterY=-87.5 CenterZ=0 NormalX=0 NormalY=0 NormalZ=1 AngleXU=0 Radius=2.5
    g23: Circle CenterX=155 CenterY=-87.5 CenterZ=0 NormalX=0 NormalY=0 NormalZ=1 AngleXU=0 Radius=2.5
    g24: Circle CenterX=0 CenterY=0 CenterZ=0 NormalX=0 NormalY=0 NormalZ=1 AngleXU=0 Radius=47.5
    g25: Circle CenterX=100 CenterY=0 CenterZ=0 NormalX=0 NormalY=0 NormalZ=1 AngleXU=0 Radius=47.5
  constraints (59):
    c: Horizontal(g0)
    c: Horizontal(g2)
    c: Vertical(g1)
    c: Vertical(g3)
    c: Tangent(g2,g4) = -1.5708
    c: Tangent(g3,g4) = -1.5708
    c: Tangent(g2,g5) = -1.5708
    c: Tangent(g1,g5) = -1.5708
    c: Tangent(g3,g6) = -1.5708
    c: Tangent(g0,g6) = -1.5708
    c: Tangent(g0,g7) = -1.5708
    c: Tangent(g1,g7) = -1.5708
    c: Equal(g4,g5)
    c: Equal(g5,g7)
    c: DistanceX(g3,g1) = 215
    c: Diameter(g4) = 96
    c: DistanceY(g0,g2) = 185
    c: Symmetric(g2,g0,g-1)
    c: Coincident(g8,g3)
    c: Coincident(g8,g1)
    c: PointOnObject(g9,g-1)
    c: PointOnObject(g9,g8)
    c: DistanceX(g-1,g9) = 50
    c: Horizontal(g15)
    c: Horizontal(g11)
    c: Vertical(g13)
    c: Vertical(g17)
    c: Tangent(g11,g10) = -1.5708
    c: Tangent(g17,g10) = -1.5708
    c: Tangent(g11,g12) = -1.5708
    c: Tangent(g13,g12) = -1.5708
    c: Tangent(g17,g16) = -1.5708
    c: Tangent(g15,g16) = -1.5708
    c: Tangent(g15,g14) = -1.5708
    c: Tangent(g13,g14) = -1.5708
    c: Equal(g10,g12)
    c: Equal(g12,g14)
    c: DistanceX(g17,g13) = 235
    c: Diameter(g10) = 25
    c: DistanceY(g15,g11) = 200
    c: Symmetric(g10,g16,g-1)
    c: Coincident(g18,g10)
    c: Coincident(g18,g14)
    c: PointOnObject(g19,g-1)
    c: PointOnObject(g19,g18)
    c: DistanceX(g-1,g19) = 50
    c: Coincident(g20,g10)
    c: Coincident(g21,g12)
    c: Coincident(g22,g16)
    c: Coincident(g23,g14)
    c: Equal(g22,g23)
    c: Equal(g23,g21)
    c: Equal(g21,g20)
    c: Diameter(g20) = 5
    c: Coincident(g24,g-1)
    c: PointOnObject(g25,g-1)
    c: DistanceX(g24,g25) = 100
    c: Equal(g25,g24)
    c: Diameter(g24) = 95
FEATURE [Sketcher::SketchObject] Sketch076
  ArcFitTolerance = 0
  AttachmentSupport = -> [XY_Plane096]
  FullyConstrained = true
  MakeInternals = false
  MapMode = 5
  expr: Constraints[14] = <<Dim_table>>.inter_shaft_len * 2.15
  expr: Constraints[15] = <<Dim_table>>.ecc_dia * 1.2
  expr: Constraints[16] = <<Dim_table>>.inter_shaft_len * 1.85
  expr: Constraints[22] = <<Dim_table>>.inter_shaft_len / 2
  expr: Constraints[37] = <<Dim_table>>.inter_shaft_len * 2.35
  expr: Constraints[38] = <<Dim_table>>.crank_dia2
  expr: Constraints[39] = <<Dim_table>>.inter_shaft_len * 2
  expr: Constraints[45] = <<Dim_table>>.inter_shaft_len / 2
  expr: Constraints[53] = <<Dim_table>>.axle_hole_dia
  sketch-geometry (24):
    g0: LineSegment StartX=-9.5 StartY=-92.5 StartZ=0 EndX=109.5 EndY=-92.5 EndZ=0
    g1: LineSegment StartX=157.5 StartY=-44.5 StartZ=0 EndX=157.5 EndY=44.5 EndZ=0
    g2: LineSegment StartX=109.5 StartY=92.5 StartZ=0 EndX=-9.5 EndY=92.5 EndZ=0
    g3: LineSegment StartX=-57.5 StartY=44.5 StartZ=0 EndX=-57.5 EndY=-44.5 EndZ=0
    g4: ArcOfCircle CenterX=-9.5 CenterY=44.5 CenterZ=0 NormalX=0 NormalY=0 NormalZ=1 AngleXU=0 Radius=48 StartAngle=1.5708 EndAngle=3.14159
    g5: ArcOfCircle CenterX=109.5 CenterY=44.5 CenterZ=0 NormalX=0 NormalY=0 NormalZ=1 AngleXU=0 Radius=48 StartAngle=0 EndAngle=1.5708
    g6: ArcOfCircle CenterX=-9.5 CenterY=-44.5 CenterZ=0 NormalX=0 NormalY=0 NormalZ=1 AngleXU=0 Radius=48 StartAngle=3.14159 EndAngle=4.71239
    g7: ArcOfCircle CenterX=109.5 CenterY=-44.5 CenterZ=0 NormalX=0 NormalY=0 NormalZ=1 AngleXU=0 Radius=48 StartAngle=4.71239 EndAngle=6.28319
    g8: LineSegment [constr] StartX=-57.5 StartY=-44.5 StartZ=0 EndX=157.5 EndY=44.5 EndZ=0
    g9: GeomPoint [constr] X=50 Y=0 Z=0
    g10: ArcOfCircle CenterX=-55 CenterY=87.5 CenterZ=0 NormalX=0 NormalY=0 NormalZ=1 AngleXU=0 Radius=12.5 StartAngle=1.5708 EndAngle=3.14159
    g11: LineSegment StartX=155 StartY=100 StartZ=0 EndX=-55 EndY=100 EndZ=0
    g12: ArcOfCircle CenterX=155 CenterY=87.5 CenterZ=0 NormalX=0 NormalY=0 NormalZ=1 AngleXU=0 Radius=12.5 StartAngle=7e-14 EndAngle=1.5708
    g13: LineSegment StartX=167.5 StartY=-87.5 StartZ=0 EndX=167.5 EndY=87.5 EndZ=0
    g14: ArcOfCircle CenterX=155 CenterY=-87.5 CenterZ=0 NormalX=0 NormalY=0 NormalZ=1 AngleXU=0 Radius=12.5 StartAngle=4.71239 EndAngle=6.28319
    g15: LineSegment StartX=-55 StartY=-100 StartZ=0 EndX=155 EndY=-100 EndZ=0
    g16: ArcOfCircle CenterX=-55 CenterY=-87.5 CenterZ=0 NormalX=0 NormalY=0 NormalZ=1 AngleXU=0 Radius=12.5 StartAngle=3.14159 EndAngle=4.71239
    g17: LineSegment StartX=-67.5 StartY=87.5 StartZ=0 EndX=-67.5 EndY=-87.5 EndZ=0
    g18: LineSegment [constr] StartX=-55 StartY=100 StartZ=0 EndX=155 EndY=-100 EndZ=0
    g19: GeomPoint [constr] X=50 Y=0 Z=0
    g20: Circle CenterX=-55 CenterY=87.5 CenterZ=0 NormalX=0 NormalY=0 NormalZ=1 AngleXU=0 Radius=2.5
    g21: Circle CenterX=155 CenterY=87.5 CenterZ=0 NormalX=0 NormalY=0 NormalZ=1 AngleXU=0 Radius=2.5
    g22: Circle CenterX=-55 CenterY=-87.5 CenterZ=0 NormalX=0 NormalY=0 NormalZ=1 AngleXU=0 Radius=2.5
    g23: Circle CenterX=155 CenterY=-87.5 CenterZ=0 NormalX=0 NormalY=0 NormalZ=1 AngleXU=0 Radius=2.5
  constraints (54):
    c: Horizontal(g0)
    c: Horizontal(g2)
    c: Vertical(g1)
    c: Vertical(g3)
    c: Tangent(g2,g4) = -1.5708
    c: Tangent(g3,g4) = -1.5708
    c: Tangent(g2,g5) = -1.5708
    c: Tangent(g1,g5) = -1.5708
    c: Tangent(g3,g6) = -1.5708
    c: Tangent(g0,g6) = -1.5708
    c: Tangent(g0,g7) = -1.5708
    c: Tangent(g1,g7) = -1.5708
    c: Equal(g4,g5)
    c: Equal(g5,g7)
    c: DistanceX(g3,g1) = 215
    c: Diameter(g4) = 96
    c: DistanceY(g0,g2) = 185
    c: Symmetric(g2,g0,g-1)
    c: Coincident(g8,g3)
    c: Coincident(g8,g1)
    c: PointOnObject(g9,g-1)
    c: PointOnObject(g9,g8)
    c: DistanceX(g-1,g9) = 50
    c: Horizontal(g15)
    c: Horizontal(g11)
    c: Vertical(g13)
    c: Vertical(g17)
    c: Tangent(g11,g10) = -1.5708
    c: Tangent(g17,g10) = -1.5708
    c: Tangent(g11,g12) = -1.5708
    c: Tangent(g13,g12) = -1.5708
    c: Tangent(g17,g16) = -1.5708
    c: Tangent(g15,g16) = -1.5708
    c: Tangent(g15,g14) = -1.5708
    c: Tangent(g13,g14) = -1.5708
    c: Equal(g10,g12)
    c: Equal(g12,g14)
    c: DistanceX(g17,g13) = 235
    c: Diameter(g10) = 25
    c: DistanceY(g15,g11) = 200
    c: Symmetric(g10,g16,g-1)
    c: Coincident(g18,g10)
    c: Coincident(g18,g14)
    c: PointOnObject(g19,g-1)
    c: PointOnObject(g19,g18)
    c: DistanceX(g-1,g19) = 50
    c: Coincident(g20,g10)
    c: Coincident(g21,g12)
    c: Coincident(g22,g16)
    c: Coincident(g23,g14)
    c: Equal(g22,g23)
    c: Equal(g23,g21)
    c: Equal(g21,g20)
    c: Diameter(g20) = 5
FEATURE [PartDesign::CoordinateSystem] LCS_Origin007
  AttacherType = Attacher::AttachEngine3D
  AttachmentSupport = -> [X_Axis094]
  MapMode = 2
FEATURE [PartDesign::Pad] Pad044
  Direction = (0,0,1)
  Length = 6
  Length2 = 10
  Profile = -> Sketch075
  ReferenceAxis = -> Sketch075 [N_Axis]
  Suppressed = false
  Type = 0
FEATURE [PartDesign::Pad] Pad045
  BaseFeature = -> Pad044
  Direction = (0,0,1)
  Length = 16.75
  Length2 = 10
  Profile = -> Sketch076
  ReferenceAxis = -> Sketch076 [N_Axis]
  Suppressed = false
  Type = 0
FEATURE [PartDesign::Body] Body_2  label="проставка_корпуса_с_шестернями"
  AllowCompound = false
  Group = -> [LCS_Origin007,Sketch075,Pad044,Sketch076,Pad045]
  Origin = -> Origin095
  Tip = -> Pad045
COMPONENT P29 — recipe-attached ("ролик 3х21.8", modeled in this document).
Construction recipe (the document's own serialized feature program — sketch geometry with constraints, then the solid features built on it; lengths are millimeters unless a unit is written):

FEATURE [PartDesign::CoordinateSystem] LCS_Origin008
  AttacherType = Attacher::AttachEngine3D
  AttachmentSupport = -> [X_Axis098]
  MapMode = 2
FEATURE [PartDesign::AdditiveCylinder] Cylinder001
  Angle = 360
  AttacherType = Attacher::AttachEngine3D
  FirstAngle = 0
  Height = 21.8
  MapMode = 1
  Radius = 1.5
  Refine = true
  SecondAngle = 0
  Suppressed = false
FEATURE [PartDesign::Body] ___________3__21_8  label="ролик 3х21.8"
  AllowCompound = false
  Group = -> [LCS_Origin008,Cylinder001]
  Origin = -> Origin099
  Tip = -> Cylinder001
COMPONENT P30 — recipe-attached ("корпус_верхний", modeled in this document).
Construction recipe (the document's own serialized feature program — sketch geometry with constraints, then the solid features built on it; lengths are millimeters unless a unit is written):

FEATURE [Sketcher::SketchObject] Sketch067
  ArcFitTolerance = 0
  AttachmentSupport = -> [XY_Plane085]
  FullyConstrained = true
  MakeInternals = false
  MapMode = 5
  expr: Constraints[14] = <<Dim_table>>.inter_shaft_len * 2.15
  expr: Constraints[15] = <<Dim_table>>.ecc_dia * 1.2
  expr: Constraints[16] = <<Dim_table>>.inter_shaft_len * 1.85
  expr: Constraints[22] = <<Dim_table>>.inter_shaft_len / 2
  expr: Constraints[37] = <<Dim_table>>.inter_shaft_len * 2.35
  expr: Constraints[38] = <<Dim_table>>.crank_dia2
  expr: Constraints[39] = <<Dim_table>>.inter_shaft_len * 2
  expr: Constraints[45] = <<Dim_table>>.inter_shaft_len / 2
  expr: Constraints[53] = <<Dim_table>>.axle_hole_dia
  expr: Constraints[56] = <<Dim_table>>.inter_shaft_len
  expr: Constraints[58] = <<Dim_table>>.crank_dia2 + <<Dim_table>>.zazor
  sketch-geometry (27):
    g0: LineSegment [constr] StartX=-9.5 StartY=-92.5 StartZ=0 EndX=109.5 EndY=-92.5 EndZ=0
    g1: LineSegment [constr] StartX=157.5 StartY=-44.5 StartZ=0 EndX=157.5 EndY=44.5 EndZ=0
    g2: LineSegment [constr] StartX=109.5 StartY=92.5 StartZ=0 EndX=-9.5 EndY=92.5 EndZ=0
    g3: LineSegment [constr] StartX=-57.5 StartY=44.5 StartZ=0 EndX=-57.5 EndY=-44.5 EndZ=0
    g4: ArcOfCircle [constr] CenterX=-9.5 CenterY=44.5 CenterZ=0 NormalX=0 NormalY=0 NormalZ=1 AngleXU=0 Radius=48 StartAngle=1.5708 EndAngle=3.14159
    g5: ArcOfCircle [constr] CenterX=109.5 CenterY=44.5 CenterZ=0 NormalX=0 NormalY=0 NormalZ=1 AngleXU=0 Radius=48 StartAngle=0 EndAngle=1.5708
    g6: ArcOfCircle [constr] CenterX=-9.5 CenterY=-44.5 CenterZ=0 NormalX=0 NormalY=0 NormalZ=1 AngleXU=0 Radius=48 StartAngle=3.14159 EndAngle=4.71239
    g7: ArcOfCircle [constr] CenterX=109.5 CenterY=-44.5 CenterZ=0 NormalX=0 NormalY=0 NormalZ=1 AngleXU=0 Radius=48 StartAngle=4.71239 EndAngle=6.28319
    g8: LineSegment [constr] StartX=-57.5 StartY=-44.5 StartZ=0 EndX=157.5 EndY=44.5 EndZ=0
    g9: GeomPoint [constr] X=50 Y=0 Z=0
    g10: ArcOfCircle CenterX=-55 CenterY=87.5 CenterZ=0 NormalX=0 NormalY=0 NormalZ=1 AngleXU=0 Radius=12.5 StartAngle=1.5708 EndAngle=3.14159
    g11: LineSegment StartX=155 StartY=100 StartZ=0 EndX=-55 EndY=100 EndZ=0
    g12: ArcOfCircle CenterX=155 CenterY=87.5 CenterZ=0 NormalX=0 NormalY=0 NormalZ=1 AngleXU=0 Radius=12.5 StartAngle=7.02e-14 EndAngle=1.5708
    g13: LineSegment StartX=167.5 StartY=-87.5 StartZ=0 EndX=167.5 EndY=87.5 EndZ=0
    g14: ArcOfCircle CenterX=155 CenterY=-87.5 CenterZ=0 NormalX=0 NormalY=0 NormalZ=1 AngleXU=0 Radius=12.5 StartAngle=4.71239 EndAngle=6.28319
    g15: LineSegment StartX=-55 StartY=-100 StartZ=0 EndX=155 EndY=-100 EndZ=0
    g16: ArcOfCircle CenterX=-55 CenterY=-87.5 CenterZ=0 NormalX=0 NormalY=0 NormalZ=1 AngleXU=0 Radius=12.5 StartAngle=3.14159 EndAngle=4.71239
    g17: LineSegment StartX=-67.5 StartY=87.5 StartZ=0 EndX=-67.5 EndY=-87.5 EndZ=0
    g18: LineSegment [constr] StartX=-55 StartY=100 StartZ=0 EndX=155 EndY=-100 EndZ=0
    g19: GeomPoint [constr] X=50 Y=0 Z=0
    g20: Circle CenterX=-55 CenterY=87.5 CenterZ=0 NormalX=0 NormalY=0 NormalZ=1 AngleXU=0 Radius=2.5
    g21: Circle CenterX=155 CenterY=87.5 CenterZ=0 NormalX=0 NormalY=0 NormalZ=1 AngleXU=0 Radius=2.5
    g22: Circle CenterX=-55 CenterY=-87.5 CenterZ=0 NormalX=0 NormalY=0 NormalZ=1 AngleXU=0 Radius=2.5
    g23: Circle CenterX=155 CenterY=-87.5 CenterZ=0 NormalX=0 NormalY=0 NormalZ=1 AngleXU=0 Radius=2.5
    g24: Circle CenterX=0 CenterY=0 CenterZ=0 NormalX=0 NormalY=0 NormalZ=1 AngleXU=0 Radius=12.75
    g25: Circle CenterX=100 CenterY=0 CenterZ=0 NormalX=0 NormalY=0 NormalZ=1 AngleXU=0 Radius=12.75
    g26: Circle CenterX=50 CenterY=0 CenterZ=0 NormalX=0 NormalY=0 NormalZ=1 AngleXU=0 Radius=12.75
  constraints (61):
    c: Horizontal(g0)
    c: Horizontal(g2)
    c: Vertical(g1)
    c: Vertical(g3)
    c: Tangent(g2,g4) = -1.5708
    c: Tangent(g3,g4) = -1.5708
    c: Tangent(g2,g5) = -1.5708
    c: Tangent(g1,g5) = -1.5708
    c: Tangent(g3,g6) = -1.5708
    c: Tangent(g0,g6) = -1.5708
    c: Tangent(g0,g7) = -1.5708
    c: Tangent(g1,g7) = -1.5708
    c: Equal(g4,g5)
    c: Equal(g5,g7)
    c: DistanceX(g3,g1) = 215
    c: Diameter(g4) = 96
    c: DistanceY(g0,g2) = 185
    c: Symmetric(g2,g0,g-1)
    c: Coincident(g8,g3)
    c: Coincident(g8,g1)
    c: PointOnObject(g9,g-1)
    c: PointOnObject(g9,g8)
    c: DistanceX(g-1,g9) = 50
    c: Horizontal(g15)
    c: Horizontal(g11)
    c: Vertical(g13)
    c: Vertical(g17)
    c: Tangent(g11,g10) = -1.5708
    c: Tangent(g17,g10) = -1.5708
    c: Tangent(g11,g12) = -1.5708
    c: Tangent(g13,g12) = -1.5708
    c: Tangent(g17,g16) = -1.5708
    c: Tangent(g15,g16) = -1.5708
    c: Tangent(g15,g14) = -1.5708
    c: Tangent(g13,g14) = -1.5708
    c: Equal(g10,g12)
    c: Equal(g12,g14)
    c: DistanceX(g17,g13) = 235
    c: Diameter(g10) = 25
    c: DistanceY(g15,g11) = 200
    c: Symmetric(g10,g16,g-1)
    c: Coincident(g18,g10)
    c: Coincident(g18,g14)
    c: PointOnObject(g19,g-1)
    c: PointOnObject(g19,g18)
    c: DistanceX(g-1,g19) = 50
    c: Coincident(g20,g10)
    c: Coincident(g21,g12)
    c: Coincident(g22,g16)
    c: Coincident(g23,g14)
    c: Equal(g22,g23)
    c: Equal(g23,g21)
    c: Equal(g21,g20)
    c: Diameter(g20) = 5
    c: Coincident(g24,g-1)
    c: PointOnObject(g25,g-1)
    c: DistanceX(g24,g25) = 100
    c: Equal(g25,g24)
    c: Diameter(g24) = 25.5
    c: Coincident(g26,g9)
    c: Equal(g24,g26)
FEATURE [PartDesign::CoordinateSystem] LCS_Origin006
  AttacherType = Attacher::AttachEngine3D
  AttachmentSupport = -> [X_Axis083]
  MapMode = 2
FEATURE [PartDesign::Pad] Pad036
  Direction = (0,0,1)
  Length = 4
  Length2 = 10
  Profile = -> Sketch067
  ReferenceAxis = -> Sketch067 [N_Axis]
  Suppressed = false
  Type = 0
FEATURE [Sketcher::SketchObject] Sketch073
  ArcFitTolerance = 0
  AttachmentSupport = -> [XY_Plane085]
  FullyConstrained = true
  MakeInternals = false
  MapMode = 5
  expr: Constraints[6] = <<Dim_table>>.crank_dia2 + <<Dim_table>>.zazor
  expr: Constraints[7] = <<Dim_table>>.crank_dia2 * 1.5
  expr: Constraints[8] = <<Dim_table>>.inter_shaft_len
  sketch-geometry (4):
    g0: Circle CenterX=0 CenterY=0 CenterZ=0 NormalX=0 NormalY=0 NormalZ=1 AngleXU=0 Radius=12.75
    g1: Circle CenterX=0 CenterY=0 CenterZ=0 NormalX=0 NormalY=0 NormalZ=1 AngleXU=0 Radius=18.75
    g2: Circle CenterX=100 CenterY=0 CenterZ=0 NormalX=0 NormalY=0 NormalZ=1 AngleXU=0 Radius=12.75
    g3: Circle CenterX=100 CenterY=0 CenterZ=0 NormalX=0 NormalY=0 NormalZ=1 AngleXU=0 Radius=18.75
  constraints (9):
    c: Coincident(g0,g-1)
    c: Coincident(g1,g0)
    c: PointOnObject(g2,g-1)
    c: Coincident(g3,g2)
    c: Equal(g0,g2)
    c: Equal(g1,g3)
    c: Diameter(g0) = 25.5
    c: Diameter(g1) = 37.5
    c: DistanceX(g-1,g2) = 100
FEATURE [PartDesign::Pad] Pad041
  BaseFeature = -> Pad036
  Direction = (0,0,1)
  Length = 10
  Length2 = 10
  Profile = -> Sketch073
  ReferenceAxis = -> Sketch073 [N_Axis]
  Suppressed = false
  Type = 0
FEATURE [PartDesign::Body] ___________________________  label="корпус_верхний"
  AllowCompound = false
  Group = -> [LCS_Origin006,Sketch067,Pad036,Sketch073,Pad041]
  Origin = -> Origin084
  Tip = -> Pad041
PROVENANCE & LICENSES
A FreeCAD (.FCStd) document from a public repository crawl; recipes are the document's own serialized feature recipes (and, for linked parts, companion documents' recipes).
License: unknown-license-file.
